FCSTD DOCUMENT  (FreeCAD 1.0R39319 (Git))
Label: assembly
License: All rights reserved
LicenseURL: https://en.wikipedia.org/wiki/All_rights_reserved
objects: App::FeaturePython×60, App::Link×19, Assembly::JointGroup×1, Assembly::AssemblyObject×1
EXTERNAL_REF file=bottom.FCStd obj=Body
EXTERNAL_REF file=side.FCStd obj=Body
EXTERNAL_REF file=speaker_panel.FCStd obj=Body
EXTERNAL_REF file=top.FCStd obj=Body
EXTERNAL_REF file=marquee.FCStd obj=Body
EXTERNAL_REF file=glass.FCStd obj=Body
EXTERNAL_REF file=front.FCStd obj=Body
EXTERNAL_REF file=fan_plane.FCStd obj=Body
EXTERNAL_REF file=ctrl_panel_front.FCStd obj=Body
EXTERNAL_REF file=ctrl_panel_bottom.FCStd obj=Body
EXTERNAL_REF file=control_panel.FCStd obj=Body
EXTERNAL_REF file=connector_panel.FCStd obj=Body
EXTERNAL_REF file=back_top_door.FCStd obj=Body
EXTERNAL_REF file=back_bottom_door.FCStd obj=Body
EXTERNAL_REF file=back_bottom.FCStd obj=Body
EXTERNAL_REF file=internal_plate.FCStd obj=Body
EXTERNAL_REF file=internal_separator.FCStd obj=Body

FEATURE [App::Link] bottom_body  label="bottom"
  LinkPlacement = pos=(397,600,85) rot=(-0.707107,0.707107,0;3.14159rad)
  LinkedObject = -> <external bottom.FCStd>#Body
  Placement = pos=(397,600,85) rot=(-0.707107,0.707107,0;3.14159rad)
FEATURE [App::Link] side_body  label="side_left"
  LinkedObject = -> <external side.FCStd>#Body
FEATURE [App::Link] speaker_panel_body  label="speaker_panel"
  LinkPlacement = pos=(345.457,-1.59533e-10,1534.51) rot=(-0.086827,-0.086827,0.992433;1.57839rad)
  LinkedObject = -> <external speaker_panel.FCStd>#Body
  Placement = pos=(345.457,-1.59533e-10,1534.51) rot=(-0.086827,-0.086827,0.992433;1.57839rad)
FEATURE [App::Link] top_body  label="top"
  LinkPlacement = pos=(147.687,600,1677) rot=(0,0,1;4.71239rad)
  LinkedObject = -> <external top.FCStd>#Body
  Placement = pos=(147.687,600,1677) rot=(0,0,1;4.71239rad)
FEATURE [App::Link] marquee_body  label="marquee"
  LinkPlacement = pos=(316.805,600,1697) rot=(-0.540716,0.540716,-0.6444;1.99673rad)
  LinkedObject = -> <external marquee.FCStd>#Body
  Placement = pos=(316.805,600,1697) rot=(-0.540716,0.540716,-0.6444;1.99673rad)
FEATURE [App::Link] Body  label="glass"
  LinkPlacement = pos=(382.714,600,967.037) rot=(0.633338,-0.633338,-0.444709;2.3047rad)
  LinkedObject = -> <external glass.FCStd>#Body
  Placement = pos=(382.714,600,967.037) rot=(0.633338,-0.633338,-0.444709;2.3047rad)
FEATURE [App::Link] front_body  label="front"
  LinkPlacement = pos=(412,-8.88241e-11,855) rot=(0,1,0;3.14159rad)
  LinkedObject = -> <external front.FCStd>#Body
  Placement = pos=(412,-8.88241e-11,855) rot=(0,1,0;3.14159rad)
FEATURE [App::Link] fan_plane_body  label="fan_plane"
  LinkPlacement = pos=(23.5142,600,1546.61) rot=(-0.357407,0.357407,0.862856;4.56541rad)
  LinkedObject = -> <external fan_plane.FCStd>#Body
  Placement = pos=(23.5142,600,1546.61) rot=(-0.357407,0.357407,0.862856;4.56541rad)
FEATURE [App::Link] ctrl_panel_body  label="ctrl_panel_front"
  LinkPlacement = pos=(551.849,600,852.879) rot=(-0.548043,0.548043,0.631899;4.26868rad)
  LinkedObject = -> <external ctrl_panel_front.FCStd>#Body
  Placement = pos=(551.849,600,852.879) rot=(-0.548043,0.548043,0.631899;4.26868rad)
FEATURE [App::Link] ctrl_panel_body001  label="ctrl_panel_bottom"
  LinkPlacement = pos=(397,600,855) rot=(0,0,1;4.71239rad)
  LinkedObject = -> <external ctrl_panel_bottom.FCStd>#Body
  Placement = pos=(397,600,855) rot=(0,0,1;4.71239rad)
FEATURE [App::Link] Body001  label="control_panel"
  LinkPlacement = pos=(568.82,-1.01012e-10,971.673) rot=(0.070712,0.070712,0.994987;1.57582rad)
  LinkedObject = -> <external control_panel.FCStd>#Body
  Placement = pos=(568.82,-1.01012e-10,971.673) rot=(0.070712,0.070712,0.994987;1.57582rad)
FEATURE [App::Link] connector_panel_body  label="connector_panel"
  LinkPlacement = pos=(17,-1.1304e-10,1086.61) rot=(0,1,0;3.14159rad)
  LinkedObject = -> <external connector_panel.FCStd>#Body
  Placement = pos=(17,-1.1304e-10,1086.61) rot=(0,1,0;3.14159rad)
FEATURE [App::FeaturePython] GroundedJoint  # Assembly grounded joint (typed FeaturePython)
  ObjectToGround = -> side_body
FEATURE [App::FeaturePython] Joint  label="Distance"  # Assembly joint (typed FeaturePython)
  Activated = true
  AngleMax = 0
  AngleMin = 0
  Detach1 = false
  Detach2 = false
  Distance = 0
  Distance2 = 0
  EnableAngleMax = false
  EnableAngleMin = false
  EnableLengthMax = false
  EnableLengthMin = false
  JointType = 5 (Distance)
  LengthMax = 0
  LengthMin = 0
  Placement1 = pos=(600,85,4.93758) rot=(-0.57735,-0.57735,0.57735;2.0944rad)
  Placement2 = pos=(224.254,-8.01027e-11,770.624) rot=(-0.57735,-0.57735,-0.57735;2.0944rad)
  Reference1 = -> Assembly [marquee_body.Face5,marquee_body.Face5]
  Reference2 = -> Assembly [side_body.Face2,side_body.Face2]
FEATURE [App::FeaturePython] Joint001  label="Parallel"  # Assembly joint (typed FeaturePython)
  Activated = true
  AngleMax = 0
  AngleMin = 0
  Detach1 = false
  Detach2 = false
  Distance = 0
  Distance2 = 0
  EnableAngleMax = false
  EnableAngleMin = false
  EnableLengthMax = false
  EnableLengthMin = false
  JointType = 6 (Parallel)
  LengthMax = 0
  LengthMin = 0
  Placement1 = pos=(346.37,-8,1615.71) rot=(0,1,0;1.39626rad)
  Placement2 = pos=(300,85,10) rot=(0,0,1;0rad)
  Reference1 = -> Assembly [side_body.Face23,side_body.Face23]
  Reference2 = -> Assembly [marquee_body.Face8,marquee_body.Face8]
FEATURE [App::FeaturePython] Joint002  label="Distance001"  # Assembly joint (typed FeaturePython)
  Activated = true
  AngleMax = 0
  AngleMin = 0
  Detach1 = false
  Detach2 = false
  Distance = -5
  Distance2 = 0
  EnableAngleMax = false
  EnableAngleMin = false
  EnableLengthMax = false
  EnableLengthMin = false
  JointType = 5 (Distance)
  LengthMax = 0
  LengthMin = 0
  Placement1 = pos=(346.37,-8,1615.71) rot=(0,1,0;1.39626rad)
  Placement2 = pos=(300,85,10) rot=(0,0,1;0rad)
  Reference1 = -> Assembly [side_body.Face23,side_body.Face23]
  Reference2 = -> Assembly [marquee_body.Face8,marquee_body.Face8]
FEATURE [App::FeaturePython] Joint003  label="Distance002"  # Assembly joint (typed FeaturePython)
  Activated = true
  AngleMax = 0
  AngleMin = 0
  Detach1 = false
  Detach2 = false
  Distance = -3
  Distance2 = 0
  EnableAngleMax = false
  EnableAngleMin = false
  EnableLengthMax = false
  EnableLengthMin = false
  JointType = 5 (Distance)
  LengthMax = 0
  LengthMin = 0
  Placement1 = pos=(235.443,-8,1700) rot=(0,0,1;0rad)
  Placement2 = pos=(300,2.274e-13,-1.137e-13) rot=(0.707107,0,0.707107;3.14159rad)
  Reference1 = -> Assembly [side_body.Face19,side_body.Face19]
  Reference2 = -> Assembly [marquee_body.Edge3,marquee_body.Edge3]
FEATURE [App::FeaturePython] Joint004  label="Distance003"  # Assembly joint (typed FeaturePython)
  Activated = true
  AngleMax = 0
  AngleMin = 0
  Detach1 = false
  Detach2 = false
  Distance = 0
  Distance2 = 0
  EnableAngleMax = false
  EnableAngleMin = false
  EnableLengthMax = false
  EnableLengthMin = false
  JointType = 5 (Distance)
  LengthMax = 0
  LengthMin = 0
  Placement1 = pos=(224.254,-8.01027e-11,770.624) rot=(-0.57735,-0.57735,-0.57735;2.0944rad)
  Placement2 = pos=(600,85,7.5) rot=(-0.57735,-0.57735,0.57735;2.0944rad)
  Reference1 = -> Assembly [side_body.Face2,side_body.Face2]
  Reference2 = -> Assembly [top_body.Face2,top_body.Face2]
FEATURE [App::FeaturePython] Joint005  label="Parallel001"  # Assembly joint (typed FeaturePython)
  Activated = true
  AngleMax = 0
  AngleMin = 0
  Detach1 = false
  Detach2 = false
  Distance = 0
  Distance2 = 0
  EnableAngleMax = false
  EnableAngleMin = false
  EnableLengthMax = false
  EnableLengthMin = false
  JointType = 6 (Parallel)
  LengthMax = 0
  LengthMin = 0
  Placement1 = pos=(300,85,15) rot=(0,0,1;0rad)
  Placement2 = pos=(235.443,-8,1700) rot=(0,0,1;0rad)
  Reference1 = -> Assembly [top_body.Face6,top_body.Face6]
  Reference2 = -> Assembly [side_body.Face19,side_body.Face19]
FEATURE [App::FeaturePython] Joint006  label="Distance004"  # Assembly joint (typed FeaturePython)
  Activated = true
  AngleMax = 0
  AngleMin = 0
  Detach1 = false
  Detach2 = false
  Distance = 8
  Distance2 = 0
  EnableAngleMax = false
  EnableAngleMin = false
  EnableLengthMax = false
  EnableLengthMin = false
  JointType = 5 (Distance)
  LengthMax = 0
  LengthMin = 0
  Placement1 = pos=(300,85,15) rot=(0,0,1;0rad)
  Placement2 = pos=(235.443,-8,1700) rot=(0,0,1;0rad)
  Reference1 = -> Assembly [top_body.Face6,top_body.Face6]
  Reference2 = -> Assembly [side_body.Face19,side_body.Face19]
FEATURE [App::FeaturePython] Joint007  label="Distance005"  # Assembly joint (typed FeaturePython)
  Activated = true
  AngleMax = 0
  AngleMin = 0
  Detach1 = false
  Detach2 = false
  Distance = 0
  Distance2 = 0
  EnableAngleMax = false
  EnableAngleMin = false
  EnableLengthMax = false
  EnableLengthMin = false
  JointType = 5 (Distance)
  LengthMax = 0
  LengthMin = 0
  Placement1 = pos=(300,85,0) rot=(0,0,1;0rad)
  Placement2 = pos=(300,170,15) rot=(-0.707107,0,0.707107;3.14159rad)
  Reference1 = -> Assembly [marquee_body.Face4,marquee_body.Face4]
  Reference2 = -> Assembly [top_body.Edge10,top_body.Edge10]
FEATURE [App::FeaturePython] Joint008  label="Distance006"  # Assembly joint (typed FeaturePython)
  Activated = true
  AngleMax = 0
  AngleMin = 0
  Detach1 = false
  Detach2 = false
  Distance = 0
  Distance2 = 0
  EnableAngleMax = false
  EnableAngleMin = false
  EnableLengthMax = false
  EnableLengthMin = false
  JointType = 5 (Distance)
  LengthMax = 0
  LengthMin = 0
  Placement1 = pos=(4.4e-15,80,7.5) rot=(-0.57735,0.57735,-0.57735;2.0944rad)
  Placement2 = pos=(224.254,-8.01027e-11,770.624) rot=(-0.57735,-0.57735,-0.57735;2.0944rad)
  Reference1 = -> Assembly [speaker_panel_body.Face4,speaker_panel_body.Face4]
  Reference2 = -> Assembly [side_body.Face2,side_body.Face2]
FEATURE [App::FeaturePython] Joint009  label="Distance007"  # Assembly joint (typed FeaturePython)
  Activated = true
  AngleMax = 0
  AngleMin = 0
  Detach1 = false
  Detach2 = false
  Distance = 0
  Distance2 = 0
  EnableAngleMax = false
  EnableAngleMin = false
  EnableLengthMax = false
  EnableLengthMin = false
  JointType = 5 (Distance)
  LengthMax = 0
  LengthMin = 0
  Placement1 = pos=(300,85,0) rot=(0,0,1;0rad)
  Placement2 = pos=(300,0,7.5) rot=(1,0,0;4.71239rad)
  Reference1 = -> Assembly [marquee_body.Face4,marquee_body.Face4]
  Reference2 = -> Assembly [speaker_panel_body.Face1,speaker_panel_body.Face1]
FEATURE [App::FeaturePython] Joint010  label="Distance008"  # Assembly joint (typed FeaturePython)
  Activated = true
  AngleMax = 0
  AngleMin = 0
  Detach1 = false
  Detach2 = false
  Distance = -5
  Distance2 = 0
  EnableAngleMax = false
  EnableAngleMin = false
  EnableLengthMax = false
  EnableLengthMin = false
  JointType = 5 (Distance)
  LengthMax = 0
  LengthMin = 0
  Placement1 = pos=(300,81.1697,-2.274e-13) rot=(0,0,1;0rad)
  Placement2 = pos=(300,170,-1.137e-13) rot=(-0.707107,0,0.707107;3.14159rad)
  Reference1 = -> Assembly [speaker_panel_body.Face7,speaker_panel_body.Face7]
  Reference2 = -> Assembly [marquee_body.Edge13,marquee_body.Edge13]
FEATURE [App::FeaturePython] Joint011  label="Distance009"  # Assembly joint (typed FeaturePython)
  Activated = true
  AngleMax = 0
  AngleMin = 0
  Detach1 = false
  Detach2 = false
  Distance = 0
  Distance2 = 0
  EnableAngleMax = false
  EnableAngleMin = false
  EnableLengthMax = false
  EnableLengthMin = false
  JointType = 5 (Distance)
  LengthMax = 0
  LengthMin = 0
  Placement1 = pos=(600,90,7.5) rot=(0.57735,0.57735,-0.57735;4.18879rad)
  Placement2 = pos=(224.254,-8.01027e-11,770.624) rot=(-0.57735,-0.57735,-0.57735;2.0944rad)
  Reference1 = -> Assembly [fan_plane_body.Face2,fan_plane_body.Face2]
  Reference2 = -> Assembly [side_body.Face2,side_body.Face2]
FEATURE [App::FeaturePython] Joint012  label="Parallel002"  # Assembly joint (typed FeaturePython)
  Activated = true
  AngleMax = 0
  AngleMin = 0
  Detach1 = false
  Detach2 = false
  Distance = 0
  Distance2 = 0
  EnableAngleMax = false
  EnableAngleMin = false
  EnableLengthMax = false
  EnableLengthMin = false
  JointType = 6 (Parallel)
  LengthMax = 0
  LengthMin = 0
  Placement1 = pos=(300,90,15) rot=(0,0,1;0rad)
  Placement2 = pos=(75,-8,1625) rot=(0,-1,0;0.785398rad)
  Reference1 = -> Assembly [fan_plane_body.Face8,fan_plane_body.Face8]
  Reference2 = -> Assembly [side_body.Face15,side_body.Face15]
FEATURE [App::FeaturePython] Joint013  label="Distance010"  # Assembly joint (typed FeaturePython)
  Activated = true
  AngleMax = 0
  AngleMin = 0
  Detach1 = false
  Detach2 = false
  Distance = 0
  Distance2 = 0
  EnableAngleMax = false
  EnableAngleMin = false
  EnableLengthMax = false
  EnableLengthMin = false
  JointType = 5 (Distance)
  LengthMax = 0
  LengthMin = 0
  Placement1 = pos=(300,90,15) rot=(0,0,1;0rad)
  Placement2 = pos=(300,0,15) rot=(0.707107,0,0.707107;3.14159rad)
  Reference1 = -> Assembly [fan_plane_body.Face8,fan_plane_body.Face8]
  Reference2 = -> Assembly [top_body.Edge4,top_body.Edge4]
FEATURE [App::FeaturePython] Joint014  label="Distance011"  # Assembly joint (typed FeaturePython)
  Activated = true
  AngleMax = 0
  AngleMin = 0
  Detach1 = false
  Detach2 = false
  Distance = 0
  Distance2 = 0
  EnableAngleMax = false
  EnableAngleMin = false
  EnableLengthMax = false
  EnableLengthMin = false
  JointType = 5 (Distance)
  LengthMax = 0
  LengthMin = 0
  Placement1 = pos=(300,180,7.5) rot=(0,-0.707107,0.707107;3.14159rad)
  Placement2 = pos=(300,0,0) rot=(0.707107,0,0.707107;3.14159rad)
  Reference1 = -> Assembly [fan_plane_body.Face3,fan_plane_body.Face3]
  Reference2 = -> Assembly [top_body.Edge3,top_body.Edge3]
FEATURE [App::FeaturePython] Joint015  label="Distance012"  # Assembly joint (typed FeaturePython)
  Activated = true
  AngleMax = 0
  AngleMin = 0
  Detach1 = false
  Detach2 = false
  Distance = 0
  Distance2 = 0
  EnableAngleMax = false
  EnableAngleMin = false
  EnableLengthMax = false
  EnableLengthMin = false
  JointType = 5 (Distance)
  LengthMax = 0
  LengthMin = 0
  Placement1 = pos=(600,190,7.5) rot=(0.57735,0.57735,-0.57735;4.18879rad)
  Placement2 = pos=(224.254,-8.01027e-11,770.624) rot=(-0.57735,-0.57735,-0.57735;2.0944rad)
  Reference1 = -> Assembly [bottom_body.Face2,bottom_body.Face2]
  Reference2 = -> Assembly [side_body.Face2,side_body.Face2]
FEATURE [App::FeaturePython] Joint016  label="Distance013"  # Assembly joint (typed FeaturePython)
  Activated = true
  AngleMax = 0
  AngleMin = 0
  Detach1 = false
  Detach2 = false
  Distance = 70
  Distance2 = 0
  EnableAngleMax = false
  EnableAngleMin = false
  EnableLengthMax = false
  EnableLengthMin = false
  JointType = 5 (Distance)
  LengthMax = 0
  LengthMin = 0
  Placement1 = pos=(300,190,15) rot=(0,0,1;0rad)
  Placement2 = pos=(225.638,-8,-8.278e-13) rot=(0,0,1;0rad)
  Reference1 = -> Assembly [bottom_body.Face6,bottom_body.Face6]
  Reference2 = -> Assembly [side_body.Face7,side_body.Face7]
FEATURE [App::FeaturePython] Joint017  label="Distance014"  # Assembly joint (typed FeaturePython)
  Activated = true
  AngleMax = 0
  AngleMin = 0
  Detach1 = false
  Detach2 = false
  Distance = 0
  Distance2 = 0
  EnableAngleMax = false
  EnableAngleMin = false
  EnableLengthMax = false
  EnableLengthMin = false
  JointType = 5 (Distance)
  LengthMax = 0
  LengthMin = 0
  Placement1 = pos=(7.5,1.6108e-11,150) rot=(0.57735,-0.57735,-0.57735;4.18879rad)
  Placement2 = pos=(224.254,-8.01027e-11,770.624) rot=(-0.57735,-0.57735,-0.57735;2.0944rad)
  Reference1 = -> Assembly [connector_panel_body.Face4,connector_panel_body.Face4]
  Reference2 = -> Assembly [side_body.Face2,side_body.Face2]
FEATURE [App::FeaturePython] Joint019  label="Parallel003"  # Assembly joint (typed FeaturePython)
  Activated = true
  AngleMax = 0
  AngleMin = 0
  Detach1 = false
  Detach2 = false
  Distance = 0
  Distance2 = 0
  EnableAngleMax = false
  EnableAngleMin = false
  EnableLengthMax = false
  EnableLengthMin = false
  JointType = 6 (Parallel)
  LengthMax = 0
  LengthMin = 0
  Placement1 = pos=(15,301.87,151.126) rot=(0.707107,0,0.707107;3.14159rad)
  Placement2 = pos=(0,-8,782.322) rot=(0,-1,0;1.5708rad)
  Reference1 = -> Assembly [connector_panel_body.Face14,connector_panel_body.Face14]
  Reference2 = -> Assembly [side_body.Face11,side_body.Face11]
FEATURE [App::FeaturePython] Joint020  label="Distance016"  # Assembly joint (typed FeaturePython)
  Activated = true
  AngleMax = 0
  AngleMin = 0
  Detach1 = false
  Detach2 = false
  Distance = 0
  Distance2 = 0
  EnableAngleMax = false
  EnableAngleMin = false
  EnableLengthMax = false
  EnableLengthMin = false
  JointType = 5 (Distance)
  LengthMax = 0
  LengthMin = 0
  Placement1 = pos=(300,380,7.5) rot=(0,0.707107,-0.707107;3.14159rad)
  Placement2 = pos=(1.69713e-11,301.87,151.126) rot=(0.707107,0,0.707107;3.14159rad)
  Reference1 = -> Assembly [bottom_body.Face3,bottom_body.Face3]
  Reference2 = -> Assembly [connector_panel_body.Face13,connector_panel_body.Face13]
FEATURE [App::FeaturePython] Joint021  label="Distance017"  # Assembly joint (typed FeaturePython)
  Activated = true
  AngleMax = 0
  AngleMin = 0
  Detach1 = false
  Detach2 = false
  Distance = 0
  Distance2 = 0
  EnableAngleMax = false
  EnableAngleMin = false
  EnableLengthMax = false
  EnableLengthMin = false
  JointType = 5 (Distance)
  LengthMax = 0
  LengthMin = 0
  Placement1 = pos=(7.5,4.71889e-11,425) rot=(0.57735,-0.57735,-0.57735;4.18879rad)
  Placement2 = pos=(224.254,-8.01027e-11,770.624) rot=(-0.57735,-0.57735,-0.57735;2.0944rad)
  Reference1 = -> Assembly [front_body.Face4,front_body.Face4]
  Reference2 = -> Assembly [side_body.Face2,side_body.Face2]
FEATURE [App::FeaturePython] Joint022  label="Distance018"  # Assembly joint (typed FeaturePython)
  Activated = true
  AngleMax = 0
  AngleMin = 0
  Detach1 = false
  Detach2 = false
  Distance = 0
  Distance2 = 0
  EnableAngleMax = false
  EnableAngleMin = false
  EnableLengthMax = false
  EnableLengthMin = false
  JointType = 5 (Distance)
  LengthMax = 0
  LengthMin = 0
  Placement1 = pos=(300,0,7.5) rot=(-1,0,0;1.5708rad)
  Placement2 = pos=(15,300,425) rot=(0.707107,0,0.707107;3.14159rad)
  Reference1 = -> Assembly [bottom_body.Face1,bottom_body.Face1]
  Reference2 = -> Assembly [front_body.Face6,front_body.Face6]
FEATURE [App::FeaturePython] Joint023  label="Distance019"  # Assembly joint (typed FeaturePython)
  Activated = true
  AngleMax = 0
  AngleMin = 0
  Detach1 = false
  Detach2 = false
  Distance = -5
  Distance2 = 0
  EnableAngleMax = false
  EnableAngleMin = false
  EnableLengthMax = false
  EnableLengthMin = false
  JointType = 5 (Distance)
  LengthMax = 0
  LengthMin = 0
  Placement1 = pos=(7.5,300,850) rot=(0.707107,-0.707107,0;3.14159rad)
  Placement2 = pos=(225.638,-8,-8.278e-13) rot=(0,0,1;0rad)
  Reference1 = -> Assembly [front_body.Face3,front_body.Face3]
  Reference2 = -> Assembly [side_body.Face7,side_body.Face7]
FEATURE [App::FeaturePython] Joint024  label="Distance020"  # Assembly joint (typed FeaturePython)
  Activated = true
  AngleMax = 0
  AngleMin = 0
  Detach1 = false
  Detach2 = false
  Distance = 0
  Distance2 = 0
  EnableAngleMax = false
  EnableAngleMin = false
  EnableLengthMax = false
  EnableLengthMin = false
  JointType = 5 (Distance)
  LengthMax = 0
  LengthMin = 0
  Placement1 = pos=(600,70,7.5) rot=(-0.57735,-0.57735,0.57735;2.0944rad)
  Placement2 = pos=(224.254,-8.01027e-11,770.624) rot=(-0.57735,-0.57735,-0.57735;2.0944rad)
  Reference1 = -> Assembly [ctrl_panel_body001.Face2,ctrl_panel_body001.Face2]
  Reference2 = -> Assembly [side_body.Face2,side_body.Face2]
FEATURE [App::FeaturePython] Joint025  label="Distance021"  # Assembly joint (typed FeaturePython)
  Activated = true
  AngleMax = 0
  AngleMin = 0
  Detach1 = false
  Detach2 = false
  Distance = 0
  Distance2 = 0
  EnableAngleMax = false
  EnableAngleMin = false
  EnableLengthMax = false
  EnableLengthMin = false
  JointType = 5 (Distance)
  LengthMax = 0
  LengthMin = 0
  Placement1 = pos=(300,69.7822,0) rot=(0,0,1;0rad)
  Placement2 = pos=(7.5,300,-3.29692e-11) rot=(0,0,1;1.5708rad)
  Reference1 = -> Assembly [ctrl_panel_body001.Face7,ctrl_panel_body001.Face7]
  Reference2 = -> Assembly [front_body.Face1,front_body.Face1]
FEATURE [App::FeaturePython] Joint026  label="Distance022"  # Assembly joint (typed FeaturePython)
  Activated = true
  AngleMax = 0
  AngleMin = 0
  Detach1 = false
  Detach2 = false
  Distance = 0
  Distance2 = 0
  EnableAngleMax = false
  EnableAngleMin = false
  EnableLengthMax = false
  EnableLengthMin = false
  JointType = 5 (Distance)
  LengthMax = 0
  LengthMin = 0
  Placement1 = pos=(300,0,7.5) rot=(-1,0,0;1.5708rad)
  Placement2 = pos=(15,300,425) rot=(0.707107,0,0.707107;3.14159rad)
  Reference1 = -> Assembly [ctrl_panel_body001.Face1,ctrl_panel_body001.Face1]
  Reference2 = -> Assembly [front_body.Face6,front_body.Face6]
FEATURE [App::FeaturePython] Joint027  label="Distance023"  # Assembly joint (typed FeaturePython)
  Activated = true
  AngleMax = 0
  AngleMin = 0
  Detach1 = false
  Detach2 = false
  Distance = 0
  Distance2 = 0
  EnableAngleMax = false
  EnableAngleMin = false
  EnableLengthMax = false
  EnableLengthMin = false
  JointType = 5 (Distance)
  LengthMax = 0
  LengthMin = 0
  Placement1 = pos=(600,60,7.5) rot=(0.57735,0.57735,-0.57735;4.18879rad)
  Placement2 = pos=(224.254,-8.01027e-11,770.624) rot=(-0.57735,-0.57735,-0.57735;2.0944rad)
  Reference1 = -> Assembly [ctrl_panel_body.Face2,ctrl_panel_body.Face2]
  Reference2 = -> Assembly [side_body.Face2,side_body.Face2]
FEATURE [App::FeaturePython] Joint028  label="Parallel024"  # Assembly joint (typed FeaturePython)
  Activated = true
  AngleMax = 0
  AngleMin = 0
  Detach1 = false
  Detach2 = false
  Distance = 0
  Distance2 = 0
  EnableAngleMax = false
  EnableAngleMin = false
  EnableLengthMax = false
  EnableLengthMin = false
  JointType = 6 (Parallel)
  LengthMax = 0
  LengthMin = 0
  Placement1 = pos=(579.262,-8,924.836) rot=(0,-1,0;1.4289rad)
  Placement2 = pos=(299.448,59.4824,1.137e-13) rot=(0,0,1;0rad)
  Reference1 = -> Assembly [side_body.Face10,side_body.Face10]
  Reference2 = -> Assembly [ctrl_panel_body.Face15,ctrl_panel_body.Face15]
FEATURE [App::FeaturePython] Joint029  label="Distance024"  # Assembly joint (typed FeaturePython)
  Activated = true
  AngleMax = 0
  AngleMin = 0
  Detach1 = false
  Detach2 = false
  Distance = 0
  Distance2 = 0
  EnableAngleMax = false
  EnableAngleMin = false
  EnableLengthMax = false
  EnableLengthMin = false
  JointType = 5 (Distance)
  LengthMax = 0
  LengthMin = 0
  Placement1 = pos=(300,69.7822,0) rot=(0,0,1;0rad)
  Placement2 = pos=(300,0,15) rot=(0.707107,0,0.707107;3.14159rad)
  Reference1 = -> Assembly [ctrl_panel_body001.Face7,ctrl_panel_body001.Face7]
  Reference2 = -> Assembly [ctrl_panel_body.Edge4,ctrl_panel_body.Edge4]
FEATURE [App::FeaturePython] Joint030  label="Distance025"  # Assembly joint (typed FeaturePython)
  Activated = true
  AngleMax = 0
  AngleMin = 0
  Detach1 = false
  Detach2 = false
  Distance = 0
  Distance2 = 0
  EnableAngleMax = false
  EnableAngleMin = false
  EnableLengthMax = false
  EnableLengthMin = false
  JointType = 5 (Distance)
  LengthMax = 0
  LengthMin = 0
  Placement1 = pos=(299.448,59.4824,15) rot=(0,0,1;0rad)
  Placement2 = pos=(300,140,0) rot=(-0.707107,0,0.707107;3.14159rad)
  Reference1 = -> Assembly [ctrl_panel_body.Face16,ctrl_panel_body.Face16]
  Reference2 = -> Assembly [ctrl_panel_body001.Edge9,ctrl_panel_body001.Edge9]
FEATURE [App::FeaturePython] Joint031  label="Distance026"  # Assembly joint (typed FeaturePython)
  Activated = true
  AngleMax = 0
  AngleMin = 0
  Detach1 = false
  Detach2 = false
  Distance = 0
  Distance2 = 0
  EnableAngleMax = false
  EnableAngleMin = false
  EnableLengthMax = false
  EnableLengthMin = false
  JointType = 5 (Distance)
  LengthMax = 0
  LengthMin = 0
  Placement1 = pos=(224.254,-8.01027e-11,770.624) rot=(-0.57735,-0.57735,-0.57735;2.0944rad)
  Placement2 = pos=(-2.17e-14,100,7.5) rot=(-0.57735,0.57735,-0.57735;2.0944rad)
  Reference1 = -> Assembly [side_body.Face2,side_body.Face2]
  Reference2 = -> Assembly [Body001.Face4,Body001.Face4]
FEATURE [App::FeaturePython] Joint032  label="Distance027"  # Assembly joint (typed FeaturePython)
  Activated = true
  AngleMax = 0
  AngleMin = 0
  Detach1 = false
  Detach2 = false
  Distance = 0
  Distance2 = 0
  EnableAngleMax = false
  EnableAngleMin = false
  EnableLengthMax = false
  EnableLengthMin = false
  JointType = 5 (Distance)
  LengthMax = 0
  LengthMin = 0
  Placement1 = pos=(300,120,7.5) rot=(0,-0.707107,0.707107;3.14159rad)
  Placement2 = pos=(298.348,98.9763,0) rot=(0,0,1;0rad)
  Reference1 = -> Assembly [ctrl_panel_body.Face3,ctrl_panel_body.Face3]
  Reference2 = -> Assembly [Body001.Face19,Body001.Face19]
FEATURE [App::FeaturePython] Joint033  label="Distance028"  # Assembly joint (typed FeaturePython)
  Activated = true
  AngleMax = 0
  AngleMin = 0
  Detach1 = false
  Detach2 = false
  Distance = 0
  Distance2 = 0
  EnableAngleMax = false
  EnableAngleMin = false
  EnableLengthMax = false
  EnableLengthMin = false
  JointType = 5 (Distance)
  LengthMax = 0
  LengthMin = 0
  Placement1 = pos=(299.448,59.4824,1.137e-13) rot=(0,0,1;0rad)
  Placement2 = pos=(300,5.68e-14,7.5) rot=(-1,0,0;1.5708rad)
  Reference1 = -> Assembly [ctrl_panel_body.Face15,ctrl_panel_body.Face15]
  Reference2 = -> Assembly [Body001.Face1,Body001.Face1]
FEATURE [App::FeaturePython] Joint034  label="Distance029"  # Assembly joint (typed FeaturePython)
  Activated = true
  AngleMax = 0
  AngleMin = 0
  Detach1 = false
  Detach2 = false
  Distance = 2
  Distance2 = 0
  EnableAngleMax = false
  EnableAngleMin = false
  EnableLengthMax = false
  EnableLengthMin = false
  JointType = 5 (Distance)
  LengthMax = 0
  LengthMin = 0
  Placement1 = pos=(15,301.87,151.126) rot=(0.707107,0,0.707107;3.14159rad)
  Placement2 = pos=(0,-8,782.322) rot=(0,-1,0;1.5708rad)
  Reference1 = -> Assembly [connector_panel_body.Face14,connector_panel_body.Face14]
  Reference2 = -> Assembly [side_body.Face11,side_body.Face11]
FEATURE [App::FeaturePython] Joint035  label="Distance030"  # Assembly joint (typed FeaturePython)
  Activated = true
  AngleMax = 0
  AngleMin = 0
  Detach1 = false
  Detach2 = false
  Distance = 0
  Distance2 = 0
  EnableAngleMax = false
  EnableAngleMin = false
  EnableLengthMax = false
  EnableLengthMin = false
  JointType = 5 (Distance)
  LengthMax = 0
  LengthMin = 0
  Placement1 = pos=(224.254,-8.01027e-11,770.624) rot=(-0.57735,-0.57735,-0.57735;2.0944rad)
  Placement2 = pos=(600,310,3) rot=(0.57735,0.57735,-0.57735;4.18879rad)
  Reference1 = -> Assembly [side_body.Face2,side_body.Face2]
  Reference2 = -> Assembly [Body.Face2,Body.Face2]
FEATURE [App::FeaturePython] Joint036  label="Distance031"  # Assembly joint (typed FeaturePython)
  Activated = true
  AngleMax = 0
  AngleMin = 0
  Detach1 = false
  Detach2 = false
  Distance = 0
  Distance2 = 0
  EnableAngleMax = false
  EnableAngleMin = false
  EnableLengthMax = false
  EnableLengthMin = false
  JointType = 5 (Distance)
  LengthMax = 0
  LengthMin = 0
  Placement1 = pos=(300,310,0) rot=(0,0,1;0rad)
  Placement2 = pos=(300,160,0) rot=(-0.707107,0,0.707107;3.14159rad)
  Reference1 = -> Assembly [Body.Face9,Body.Face9]
  Reference2 = -> Assembly [speaker_panel_body.Edge9,speaker_panel_body.Edge9]
FEATURE [App::FeaturePython] Joint037  label="Distance032"  # Assembly joint (typed FeaturePython)
  Activated = true
  AngleMax = 0
  AngleMin = 0
  Detach1 = false
  Detach2 = false
  Distance = 0
  Distance2 = 0
  EnableAngleMax = false
  EnableAngleMin = false
  EnableLengthMax = false
  EnableLengthMin = false
  JointType = 5 (Distance)
  LengthMax = 0
  LengthMin = 0
  Placement1 = pos=(300,310,0) rot=(0,0,1;0rad)
  Placement2 = pos=(300,200,0) rot=(-0.707107,0,0.707107;3.14159rad)
  Reference1 = -> Assembly [Body.Face9,Body.Face9]
  Reference2 = -> Assembly [Body001.Edge9,Body001.Edge9]
FEATURE [App::Link] Body002  label="back_top_door"
  LinkPlacement = pos=(17,-1.6069e-10,1546.61) rot=(0.707107,0.707107,0;3.14159rad)
  LinkedObject = -> <external back_top_door.FCStd>#Body
  Placement = pos=(17,-1.6069e-10,1546.61) rot=(0.707107,0.707107,0;3.14159rad)
FEATURE [App::FeaturePython] Joint039  label="Distance034"  # Assembly joint (typed FeaturePython)
  Activated = true
  AngleMax = 0
  AngleMin = 0
  Detach1 = false
  Detach2 = false
  Distance = 0
  Distance2 = 0
  EnableAngleMax = false
  EnableAngleMin = false
  EnableLengthMax = false
  EnableLengthMin = false
  JointType = 5 (Distance)
  LengthMax = 0
  LengthMin = 0
  Placement1 = pos=(0,-7.5,230) rot=(0,-1,0;4.71239rad)
  Placement2 = pos=(224.254,-8.01027e-11,770.624) rot=(-0.57735,-0.57735,-0.57735;2.0944rad)
  Reference1 = -> Assembly [Body002.Face4,Body002.Face4]
  Reference2 = -> Assembly [side_body.Face2,side_body.Face2]
FEATURE [App::FeaturePython] Joint040  label="Distance035"  # Assembly joint (typed FeaturePython)
  Activated = true
  AngleMax = 0
  AngleMin = 0
  Detach1 = false
  Detach2 = false
  Distance = 0
  Distance2 = 0
  EnableAngleMax = false
  EnableAngleMin = false
  EnableLengthMax = false
  EnableLengthMin = false
  JointType = 5 (Distance)
  LengthMax = 0
  LengthMin = 0
  Placement1 = pos=(300,-15,230) rot=(-0.57735,-0.57735,-0.57735;2.0944rad)
  Placement2 = pos=(15,301.87,151.126) rot=(0.707107,0,0.707107;3.14159rad)
  Reference1 = -> Assembly [Body002.Face6,Body002.Face6]
  Reference2 = -> Assembly [connector_panel_body.Face14,connector_panel_body.Face14]
FEATURE [App::FeaturePython] Joint041  label="Distance036"  # Assembly joint (typed FeaturePython)
  Activated = true
  AngleMax = 0
  AngleMin = 0
  Detach1 = false
  Detach2 = false
  Distance = 0
  Distance2 = 0
  EnableAngleMax = false
  EnableAngleMin = false
  EnableLengthMax = false
  EnableLengthMin = false
  JointType = 5 (Distance)
  LengthMax = 0
  LengthMin = 0
  Placement1 = pos=(300,-7.5,0) rot=(0,0,1;0rad)
  Placement2 = pos=(300,0,0) rot=(0.707107,0,0.707107;3.14159rad)
  Reference1 = -> Assembly [Body002.Face1,Body002.Face1]
  Reference2 = -> Assembly [fan_plane_body.Edge3,fan_plane_body.Edge3]
FEATURE [App::FeaturePython] Joint042  label="Distance037"  # Assembly joint (typed FeaturePython)
  Activated = true
  AngleMax = 0
  AngleMin = 0
  Detach1 = false
  Detach2 = false
  Distance = 0
  Distance2 = 0
  EnableAngleMax = false
  EnableAngleMin = false
  EnableLengthMax = false
  EnableLengthMin = false
  JointType = 5 (Distance)
  LengthMax = 0
  LengthMin = 0
  Placement1 = pos=(7.5,300,-3.29692e-11) rot=(0,0,1;1.5708rad)
  Placement2 = pos=(300,-7.5,460) rot=(0,-1,0;3.14159rad)
  Reference1 = -> Assembly [connector_panel_body.Face1,connector_panel_body.Face1]
  Reference2 = -> Assembly [Body002.Face3,Body002.Face3]
FEATURE [App::Link] back_bottom_door_body  label="back_bottom_door"
  LinkPlacement = pos=(17,-8.17396e-11,786.614) rot=(0.707107,0.707107,0;3.14159rad)
  LinkedObject = -> <external back_bottom_door.FCStd>#Body
  Placement = pos=(17,-8.17396e-11,786.614) rot=(0.707107,0.707107,0;3.14159rad)
FEATURE [App::FeaturePython] Joint043  label="Distance038"  # Assembly joint (typed FeaturePython)
  Activated = true
  AngleMax = 0
  AngleMin = 0
  Detach1 = false
  Detach2 = false
  Distance = 0
  Distance2 = 0
  EnableAngleMax = false
  EnableAngleMin = false
  EnableLengthMax = false
  EnableLengthMin = false
  JointType = 5 (Distance)
  LengthMax = 0
  LengthMin = 0
  Placement1 = pos=(0,-7.5,215) rot=(0,-1,0;4.71239rad)
  Placement2 = pos=(224.254,-8.01027e-11,770.624) rot=(-0.57735,-0.57735,-0.57735;2.0944rad)
  Reference1 = -> Assembly [back_bottom_door_body.Face4,back_bottom_door_body.Face4]
  Reference2 = -> Assembly [side_body.Face2,side_body.Face2]
FEATURE [App::FeaturePython] Joint044  label="Distance039"  # Assembly joint (typed FeaturePython)
  Activated = true
  AngleMax = 0
  AngleMin = 0
  Detach1 = false
  Detach2 = false
  Distance = 0
  Distance2 = 0
  EnableAngleMax = false
  EnableAngleMin = false
  EnableLengthMax = false
  EnableLengthMin = false
  JointType = 5 (Distance)
  LengthMax = 0
  LengthMin = 0
  Placement1 = pos=(300,-15,215) rot=(-0.57735,-0.57735,-0.57735;2.0944rad)
  Placement2 = pos=(15,301.87,151.126) rot=(0.707107,0,0.707107;3.14159rad)
  Reference1 = -> Assembly [back_bottom_door_body.Face6,back_bottom_door_body.Face6]
  Reference2 = -> Assembly [connector_panel_body.Face14,connector_panel_body.Face14]
FEATURE [App::FeaturePython] Joint045  label="Distance040"  # Assembly joint (typed FeaturePython)
  Activated = true
  AngleMax = 0
  AngleMin = 0
  Detach1 = false
  Detach2 = false
  Distance = 0
  Distance2 = 0
  EnableAngleMax = false
  EnableAngleMin = false
  EnableLengthMax = false
  EnableLengthMin = false
  JointType = 5 (Distance)
  LengthMax = 0
  LengthMin = 0
  Placement1 = pos=(7.5,300,300) rot=(0.707107,-0.707107,0;3.14159rad)
  Placement2 = pos=(300,-7.5,0) rot=(0,0,1;0rad)
  Reference1 = -> Assembly [connector_panel_body.Face3,connector_panel_body.Face3]
  Reference2 = -> Assembly [back_bottom_door_body.Face1,back_bottom_door_body.Face1]
FEATURE [App::Link] back_bottom_body  label="back_subwoffer_door"
  LinkPlacement = pos=(17,-3.70479e-11,356.614) rot=(0.707107,0.707107,0;3.14159rad)
  LinkedObject = -> <external back_bottom.FCStd>#Body
  Placement = pos=(17,-3.70479e-11,356.614) rot=(0.707107,0.707107,0;3.14159rad)
FEATURE [App::FeaturePython] Joint046  label="Distance041"  # Assembly joint (typed FeaturePython)
  Activated = true
  AngleMax = 0
  AngleMin = 0
  Detach1 = false
  Detach2 = false
  Distance = 0
  Distance2 = 0
  EnableAngleMax = false
  EnableAngleMin = false
  EnableLengthMax = false
  EnableLengthMin = false
  JointType = 5 (Distance)
  LengthMax = 0
  LengthMin = 0
  Placement1 = pos=(0,-7.5,145) rot=(0,-1,0;4.71239rad)
  Placement2 = pos=(224.254,-8.01027e-11,770.624) rot=(-0.57735,-0.57735,-0.57735;2.0944rad)
  Reference1 = -> Assembly [back_bottom_body.Face4,back_bottom_body.Face4]
  Reference2 = -> Assembly [side_body.Face2,side_body.Face2]
FEATURE [App::FeaturePython] Joint047  label="Distance042"  # Assembly joint (typed FeaturePython)
  Activated = true
  AngleMax = 0
  AngleMin = 0
  Detach1 = false
  Detach2 = false
  Distance = 0
  Distance2 = 0
  EnableAngleMax = false
  EnableAngleMin = false
  EnableLengthMax = false
  EnableLengthMin = false
  JointType = 5 (Distance)
  LengthMax = 0
  LengthMin = 0
  Placement1 = pos=(300,-7.5,0) rot=(0,0,1;0rad)
  Placement2 = pos=(300,-7.5,430) rot=(0,-1,0;3.14159rad)
  Reference1 = -> Assembly [back_bottom_body.Face1,back_bottom_body.Face1]
  Reference2 = -> Assembly [back_bottom_door_body.Face3,back_bottom_door_body.Face3]
FEATURE [App::FeaturePython] Joint048  label="Distance043"  # Assembly joint (typed FeaturePython)
  Activated = true
  AngleMax = 0
  AngleMin = 0
  Detach1 = false
  Detach2 = false
  Distance = 0
  Distance2 = 0
  EnableAngleMax = false
  EnableAngleMin = false
  EnableLengthMax = false
  EnableLengthMin = false
  JointType = 5 (Distance)
  LengthMax = 0
  LengthMin = 0
  Placement1 = pos=(300,-15,145) rot=(-0.57735,-0.57735,-0.57735;2.0944rad)
  Placement2 = pos=(300,-15,215) rot=(-0.57735,-0.57735,-0.57735;2.0944rad)
  Reference1 = -> Assembly [back_bottom_body.Face6,back_bottom_body.Face6]
  Reference2 = -> Assembly [back_bottom_door_body.Face6,back_bottom_door_body.Face6]
FEATURE [App::Link] internal_plate_body  label="internal_plate"
  LinkPlacement = pos=(397,-8.2639e-11,795) rot=(-0.57735,-0.57735,0.57735;2.0944rad)
  LinkedObject = -> <external internal_plate.FCStd>#Body
  Placement = pos=(397,-8.2639e-11,795) rot=(-0.57735,-0.57735,0.57735;2.0944rad)
FEATURE [App::FeaturePython] Joint049  label="Distance044"  # Assembly joint (typed FeaturePython)
  Activated = true
  AngleMax = 0
  AngleMin = 0
  Detach1 = false
  Detach2 = false
  Distance = 0
  Distance2 = 0
  EnableAngleMax = false
  EnableAngleMin = false
  EnableLengthMax = false
  EnableLengthMin = false
  JointType = 5 (Distance)
  LengthMax = 0
  LengthMin = 0
  Placement1 = pos=(-3.75e-14,-7.5,110) rot=(0,-1,0;4.71239rad)
  Placement2 = pos=(224.254,-8.01027e-11,770.624) rot=(-0.57735,-0.57735,-0.57735;2.0944rad)
  Reference1 = -> Assembly [internal_plate_body.Face4,internal_plate_body.Face4]
  Reference2 = -> Assembly [side_body.Face2,side_body.Face2]
FEATURE [App::FeaturePython] Joint050  label="Distance045"  # Assembly joint (typed FeaturePython)
  Activated = true
  AngleMax = 0
  AngleMin = 0
  Detach1 = false
  Detach2 = false
  Distance = -60
  Distance2 = 0
  EnableAngleMax = false
  EnableAngleMin = false
  EnableLengthMax = false
  EnableLengthMin = false
  JointType = 5 (Distance)
  LengthMax = 0
  LengthMin = 0
  Placement1 = pos=(300,-15,110) rot=(-0.57735,-0.57735,-0.57735;2.0944rad)
  Placement2 = pos=(300,69.7822,15) rot=(0,0,1;0rad)
  Reference1 = -> Assembly [internal_plate_body.Face6,internal_plate_body.Face6]
  Reference2 = -> Assembly [ctrl_panel_body001.Face8,ctrl_panel_body001.Face8]
FEATURE [App::FeaturePython] Joint051  label="Distance046"  # Assembly joint (typed FeaturePython)
  Activated = true
  AngleMax = 0
  AngleMin = 0
  Detach1 = false
  Detach2 = false
  Distance = 0
  Distance2 = 0
  EnableAngleMax = false
  EnableAngleMin = false
  EnableLengthMax = false
  EnableLengthMin = false
  JointType = 5 (Distance)
  LengthMax = 0
  LengthMin = 0
  Placement1 = pos=(300,-7.5,1.137e-13) rot=(0,0,1;0rad)
  Placement2 = pos=(15,300,425) rot=(0.707107,0,0.707107;3.14159rad)
  Reference1 = -> Assembly [internal_plate_body.Face1,internal_plate_body.Face1]
  Reference2 = -> Assembly [front_body.Face6,front_body.Face6]
FEATURE [App::Link] internal_separator_body  label="internal_separator"
  LinkPlacement = pos=(192,-8.26865e-11,795) rot=(0.707107,0.707107,0;3.14159rad)
  LinkedObject = -> <external internal_separator.FCStd>#Body
  Placement = pos=(192,-8.26865e-11,795) rot=(0.707107,0.707107,0;3.14159rad)
FEATURE [App::FeaturePython] Joint052  label="Distance047"  # Assembly joint (typed FeaturePython)
  Activated = true
  AngleMax = 0
  AngleMin = 0
  Detach1 = false
  Detach2 = false
  Distance = 0
  Distance2 = 0
  EnableAngleMax = false
  EnableAngleMin = false
  EnableLengthMax = false
  EnableLengthMin = false
  JointType = 5 (Distance)
  LengthMax = 0
  LengthMin = 0
  Placement1 = pos=(0,-7.5,250) rot=(0,-1,0;4.71239rad)
  Placement2 = pos=(224.254,-8.01027e-11,770.624) rot=(-0.57735,-0.57735,-0.57735;2.0944rad)
  Reference1 = -> Assembly [internal_separator_body.Face4,internal_separator_body.Face4]
  Reference2 = -> Assembly [side_body.Face2,side_body.Face2]
FEATURE [App::FeaturePython] Joint053  label="Distance048"  # Assembly joint (typed FeaturePython)
  Activated = true
  AngleMax = 0
  AngleMin = 0
  Detach1 = false
  Detach2 = false
  Distance = 0
  Distance2 = 0
  EnableAngleMax = false
  EnableAngleMin = false
  EnableLengthMax = false
  EnableLengthMin = false
  JointType = 5 (Distance)
  LengthMax = 0
  LengthMin = 0
  Placement1 = pos=(300,-7.5,1.137e-13) rot=(0,0,1;0rad)
  Placement2 = pos=(300,-1.137e-13,110) rot=(-0.57735,-0.57735,-0.57735;2.0944rad)
  Reference1 = -> Assembly [internal_separator_body.Face1,internal_separator_body.Face1]
  Reference2 = -> Assembly [internal_plate_body.Face5,internal_plate_body.Face5]
FEATURE [App::FeaturePython] Joint054  label="Distance049"  # Assembly joint (typed FeaturePython)
  Activated = true
  AngleMax = 0
  AngleMin = 0
  Detach1 = false
  Detach2 = false
  Distance = 0
  Distance2 = 0
  EnableAngleMax = false
  EnableAngleMin = false
  EnableLengthMax = false
  EnableLengthMin = false
  JointType = 5 (Distance)
  LengthMax = 0
  LengthMin = 0
  Placement1 = pos=(300,-15,250) rot=(-0.57735,-0.57735,-0.57735;2.0944rad)
  Placement2 = pos=(300,-7.5,220) rot=(0,-1,0;3.14159rad)
  Reference1 = -> Assembly [internal_separator_body.Face6,internal_separator_body.Face6]
  Reference2 = -> Assembly [internal_plate_body.Face3,internal_plate_body.Face3]
FEATURE [App::Link] side_body001  label="side_right"
  LinkPlacement = pos=(-2.336e-13,616,6.40146e-11) rot=(0,0,1;0rad)
  LinkedObject = -> <external side.FCStd>#Body
  Placement = pos=(-2.336e-13,616,6.40146e-11) rot=(0,0,1;0rad)
FEATURE [App::FeaturePython] Joint055  label="Distance050"  # Assembly joint (typed FeaturePython)
  Activated = true
  AngleMax = 0
  AngleMin = 0
  Detach1 = false
  Detach2 = false
  Distance = 0
  Distance2 = 0
  EnableAngleMax = false
  EnableAngleMin = false
  EnableLengthMax = false
  EnableLengthMin = false
  JointType = 5 (Distance)
  LengthMax = 0
  LengthMin = 0
  Placement1 = pos=(0,-8,782.322) rot=(0,-1,0;1.5708rad)
  Placement2 = pos=(0,-8,782.322) rot=(0,-1,0;1.5708rad)
  Reference1 = -> Assembly [side_body001.Face11,side_body001.Face11]
  Reference2 = -> Assembly [side_body.Face11,side_body.Face11]
FEATURE [App::FeaturePython] Joint056  label="Distance051"  # Assembly joint (typed FeaturePython)
  Activated = true
  AngleMax = 0
  AngleMin = 0
  Detach1 = false
  Detach2 = false
  Distance = 0
  Distance2 = 0
  EnableAngleMax = false
  EnableAngleMin = false
  EnableLengthMax = false
  EnableLengthMin = false
  JointType = 5 (Distance)
  LengthMax = 0
  LengthMin = 0
  Placement1 = pos=(225.638,-8,-8.278e-13) rot=(0,0,1;0rad)
  Placement2 = pos=(225.638,-8,-8.278e-13) rot=(0,0,1;0rad)
  Reference1 = -> Assembly [side_body001.Face7,side_body001.Face7]
  Reference2 = -> Assembly [side_body.Face7,side_body.Face7]
FEATURE [App::FeaturePython] Joint057  label="Distance052"  # Assembly joint (typed FeaturePython)
  Activated = true
  AngleMax = 0
  AngleMin = 0
  Detach1 = false
  Detach2 = false
  Distance = 0
  Distance2 = 0
  EnableAngleMax = false
  EnableAngleMin = false
  EnableLengthMax = false
  EnableLengthMin = false
  JointType = 5 (Distance)
  LengthMax = 0
  LengthMin = 0
  Placement1 = pos=(224.254,-16,770.624) rot=(-0.57735,-0.57735,-0.57735;2.0944rad)
  Placement2 = pos=(0,190,7.5) rot=(-0.57735,0.57735,-0.57735;2.0944rad)
  Reference1 = -> Assembly [side_body001.Face5,side_body001.Face5]
  Reference2 = -> Assembly [bottom_body.Face4,bottom_body.Face4]
FEATURE [App::Link] bottom_body001  label="subwoofer_top"
  LinkPlacement = pos=(17,-3.06703e-11,295) rot=(0.707107,0.707107,0;3.14159rad)
  LinkedObject = -> <external bottom.FCStd>#Body
  Placement = pos=(17,-3.06703e-11,295) rot=(0.707107,0.707107,0;3.14159rad)
FEATURE [App::FeaturePython] Joint058  label="Longueur"  # Assembly joint (typed FeaturePython)
  Activated = true
  AngleMax = 0
  AngleMin = 0
  Detach1 = false
  Detach2 = false
  Distance = 0
  Distance2 = 0
  EnableAngleMax = false
  EnableAngleMin = false
  EnableLengthMax = false
  EnableLengthMin = false
  JointType = 5 (Distance)
  LengthMax = 0
  LengthMin = 0
  Placement1 = pos=(224.254,-8.01027e-11,770.624) rot=(-0.57735,-0.57735,-0.57735;2.0944rad)
  Placement2 = pos=(0,190,7.5) rot=(-0.57735,0.57735,-0.57735;2.0944rad)
  Reference1 = -> Assembly [side_body.Fillet001.Face2,side_body.Fillet001.Face2]
  Reference2 = -> Assembly [bottom_body001.Pad.Face4,bottom_body001.Pad.Face4]
FEATURE [App::FeaturePython] Joint059  label="Longueur001"  # Assembly joint (typed FeaturePython)
  Activated = true
  AngleMax = 0
  AngleMin = 0
  Detach1 = false
  Detach2 = false
  Distance = 0
  Distance2 = 0
  EnableAngleMax = false
  EnableAngleMin = false
  EnableLengthMax = false
  EnableLengthMin = false
  JointType = 5 (Distance)
  LengthMax = 0
  LengthMin = 0
  Placement1 = pos=(300,190,0) rot=(0,0,1;0rad)
  Placement2 = pos=(300,-7.5,500) rot=(0,-1,0;3.14159rad)
  Reference1 = -> Assembly [bottom_body001.Pad.Face5,bottom_body001.Pad.Face5]
  Reference2 = -> Assembly [internal_separator_body.Pad.Face3,internal_separator_body.Pad.Face3]
FEATURE [App::FeaturePython] Joint060  label="Longueur002"  # Assembly joint (typed FeaturePython)
  Activated = true
  AngleMax = 0
  AngleMin = 0
  Detach1 = false
  Detach2 = false
  Distance = 0
  Distance2 = 0
  EnableAngleMax = false
  EnableAngleMin = false
  EnableLengthMax = false
  EnableLengthMin = false
  JointType = 5 (Distance)
  LengthMax = 0
  LengthMin = 0
  Placement1 = pos=(300,380,7.5) rot=(0,-0.707107,0.707107;3.14159rad)
  Placement2 = pos=(15,300,425) rot=(0.707107,0,0.707107;3.14159rad)
  Reference1 = -> Assembly [bottom_body001.Pad.Face3,bottom_body001.Pad.Face3]
  Reference2 = -> Assembly [front_body.Pad.Face6,front_body.Pad.Face6]
FEATURE [Assembly::JointGroup] Joints
  Group = -> [GroundedJoint,Joint,Joint001,Joint002,Joint003,Joint004,Joint005,Joint006,Joint007,Joint008,Joint009,Joint010,Joint011,Joint012,Joint013,Joint014,Joint015,Joint016,Joint017,Joint019,Joint020,Joint021,Joint022,Joint023,Joint024,Joint025,Joint026,Joint027,Joint028,Joint029,Joint030,Joint031,Joint032,Joint033,Joint034,Joint035,Joint036,Joint037,Joint039,Joint040,Joint041,Joint042,Joint043,Joint044,+16 more]
FEATURE [Assembly::AssemblyObject] Assembly
  Group = -> [Joints,bottom_body,side_body,speaker_panel_body,top_body,marquee_body,Body,front_body,fan_plane_body,ctrl_panel_body,ctrl_panel_body001,Body001,connector_panel_body,GroundedJoint,Joint,Joint001,Joint002,Joint003,Joint004,Joint005,Joint006,Joint007,Joint008,Joint009,Joint010,Joint011,Joint012,Joint013,Joint014,Joint015,Joint016,Joint017,Joint019,Joint020,Joint021,Joint022,Joint023,Joint024,+42 more]
  Origin = -> Origin
  Type = Assembly

RESOLVED EXTERNAL PARTS (link-assembly join: the EXTERNAL_REF files above that resolve inside this repo's crawl, each included once):
---- part back_bottom.FCStd = doc fcstd_d52e2de3eea4 ----
FCSTD DOCUMENT  (FreeCAD 1.0R39319 (Git))
Label: back_bottom
License: All rights reserved
LicenseURL: https://en.wikipedia.org/wiki/All_rights_reserved
objects: Sketcher::SketchObject×1, PartDesign::Pad×1, PartDesign::Body×1
note: 6 computed .brp shape members not serialized (recipe doc carries the construction recipe); baked Part::Feature solids carry a one-line shape summary decoded from their .brp

FEATURE [Sketcher::SketchObject] Sketch  label="back_bottom_s"
  ArcFitTolerance = 1e-06
  AttachmentSupport = -> [XZ_Plane]
  FullyConstrained = true
  MakeInternals = false
  MapMode = 5
  Placement = pos=(0,0,0) rot=(1,0,0;1.5708rad)
  sketch-geometry (4):
    g0: LineSegment StartX=0 StartY=0 StartZ=0 EndX=600 EndY=0 EndZ=0
    g1: LineSegment StartX=600 StartY=0 StartZ=0 EndX=600 EndY=290 EndZ=0
    g2: LineSegment StartX=600 StartY=290 StartZ=0 EndX=0 EndY=290 EndZ=0
    g3: LineSegment StartX=0 StartY=290 StartZ=0 EndX=0 EndY=0 EndZ=0
  constraints (11):
    c: Coincident(g0,g1)
    c: Coincident(g1,g2)
    c: Coincident(g2,g3)
    c: Coincident(g3,g0)
    c: Horizontal(g0)
    c: Horizontal(g2)
    c: Vertical(g1)
    c: Vertical(g3)
    c: Coincident(g0,g-1)
    c: DistanceX(g2,g2) = 600
    c: DistanceY(g3,g3) = 290
FEATURE [PartDesign::Pad] Pad  label="back_bottom"
  Direction = (0,-1,2e-16)
  Length = 15
  Length2 = 10
  Placement = pos=(0,0,0) rot=(1,0,0;1.5708rad)
  Profile = -> Sketch
  ReferenceAxis = -> Sketch [N_Axis]
  Refine = true
  Suppressed = false
  Type = 0
FEATURE [PartDesign::Body] Body  label="back_bottom_body"
  AllowCompound = false
  Group = -> [Sketch,Pad]
  Origin = -> Origin
  Tip = -> Pad
---- part back_bottom_door.FCStd = doc fcstd_a515aa9ce11e ----
FCSTD DOCUMENT  (FreeCAD 1.0R39319 (Git))
Label: back_bottom_door
License: All rights reserved
LicenseURL: https://en.wikipedia.org/wiki/All_rights_reserved
objects: Sketcher::SketchObject×1, PartDesign::Pad×1, PartDesign::Body×1
note: 6 computed .brp shape members not serialized (recipe doc carries the construction recipe); baked Part::Feature solids carry a one-line shape summary decoded from their .brp

FEATURE [Sketcher::SketchObject] Sketch  label="back_bottom_door_s"
  ArcFitTolerance = 1e-06
  AttachmentSupport = -> [XZ_Plane]
  FullyConstrained = true
  MakeInternals = false
  MapMode = 5
  Placement = pos=(0,0,0) rot=(1,0,0;1.5708rad)
  sketch-geometry (4):
    g0: LineSegment StartX=0 StartY=0 StartZ=0 EndX=600 EndY=0 EndZ=0
    g1: LineSegment StartX=600 StartY=0 StartZ=0 EndX=600 EndY=430 EndZ=0
    g2: LineSegment StartX=600 StartY=430 StartZ=0 EndX=0 EndY=430 EndZ=0
    g3: LineSegment StartX=0 StartY=430 StartZ=0 EndX=0 EndY=0 EndZ=0
  constraints (11):
    c: Coincident(g0,g1)
    c: Coincident(g1,g2)
    c: Coincident(g2,g3)
    c: Coincident(g3,g0)
    c: Horizontal(g0)
    c: Horizontal(g2)
    c: Vertical(g1)
    c: Vertical(g3)
    c: Coincident(g0,g-1)
    c: DistanceX(g2,g2) = 600
    c: DistanceY(g3,g3) = 430
FEATURE [PartDesign::Pad] Pad  label="back_bottom_door"
  Direction = (0,-1,2e-16)
  Length = 15
  Length2 = 10
  Placement = pos=(0,0,0) rot=(1,0,0;1.5708rad)
  Profile = -> Sketch
  ReferenceAxis = -> Sketch [N_Axis]
  Refine = true
  Suppressed = false
  Type = 0
FEATURE [PartDesign::Body] Body  label="back_bottom_door_body"
  AllowCompound = false
  Group = -> [Sketch,Pad]
  Origin = -> Origin
  Tip = -> Pad
---- part back_top_door.FCStd = doc fcstd_c87b5e8a9fea ----
FCSTD DOCUMENT  (FreeCAD 1.0R39319 (Git))
Label: back_top_door
License: All rights reserved
LicenseURL: https://en.wikipedia.org/wiki/All_rights_reserved
objects: Sketcher::SketchObject×1, PartDesign::Pad×1, PartDesign::Body×1
note: 6 computed .brp shape members not serialized (recipe doc carries the construction recipe); baked Part::Feature solids carry a one-line shape summary decoded from their .brp

FEATURE [Sketcher::SketchObject] Sketch  label="back_top_door_s"
  ArcFitTolerance = 1e-06
  AttachmentSupport = -> [XZ_Plane]
  FullyConstrained = true
  MakeInternals = false
  MapMode = 5
  Placement = pos=(0,0,0) rot=(1,0,0;1.5708rad)
  sketch-geometry (4):
    g0: LineSegment StartX=0 StartY=0 StartZ=0 EndX=600 EndY=0 EndZ=0
    g1: LineSegment StartX=600 StartY=0 StartZ=0 EndX=600 EndY=460 EndZ=0
    g2: LineSegment StartX=600 StartY=460 StartZ=0 EndX=0 EndY=460 EndZ=0
    g3: LineSegment StartX=0 StartY=460 StartZ=0 EndX=0 EndY=0 EndZ=0
  constraints (11):
    c: Coincident(g0,g1)
    c: Coincident(g1,g2)
    c: Coincident(g2,g3)
    c: Coincident(g3,g0)
    c: Horizontal(g0)
    c: Horizontal(g2)
    c: Vertical(g1)
    c: Vertical(g3)
    c: Coincident(g0,g-1)
    c: DistanceX(g2,g2) = 600
    c: DistanceY(g3,g3) = 460
FEATURE [PartDesign::Pad] Pad  label="back_top_door"
  Direction = (0,-1,2e-16)
  Length = 15
  Length2 = 10
  Placement = pos=(0,0,0) rot=(1,0,0;1.5708rad)
  Profile = -> Sketch
  ReferenceAxis = -> Sketch [N_Axis]
  Refine = true
  Suppressed = false
  Type = 0
FEATURE [PartDesign::Body] Body  label="back_top_door_body"
  AllowCompound = false
  Group = -> [Sketch,Pad]
  Origin = -> Origin
  Tip = -> Pad
---- part bottom.FCStd = doc fcstd_0f6f75d44551 ----
FCSTD DOCUMENT  (FreeCAD 1.0R39319 (Git))
Label: bottom
License: All rights reserved
LicenseURL: http://en.wikipedia.org/wiki/All_rights_reserved
objects: Sketcher::SketchObject×1, PartDesign::Pad×1, PartDesign::Body×1
note: 6 computed .brp shape members not serialized (recipe doc carries the construction recipe); baked Part::Feature solids carry a one-line shape summary decoded from their .brp

FEATURE [Sketcher::SketchObject] Sketch  label="bottom_sketch"
  ArcFitTolerance = 0
  AttachmentSupport = -> [XY_Plane]
  FullyConstrained = true
  MakeInternals = false
  MapMode = 5
  sketch-geometry (4):
    g0: LineSegment StartX=0 StartY=0 StartZ=0 EndX=600 EndY=0 EndZ=0
    g1: LineSegment StartX=600 StartY=0 StartZ=0 EndX=600 EndY=380 EndZ=0
    g2: LineSegment StartX=600 StartY=380 StartZ=0 EndX=0 EndY=380 EndZ=0
    g3: LineSegment StartX=0 StartY=380 StartZ=0 EndX=0 EndY=0 EndZ=0
  constraints (11):
    c: Coincident(g0,g1)
    c: Coincident(g1,g2)
    c: Coincident(g2,g3)
    c: Coincident(g3,g0)
    c: Horizontal(g0)
    c: Horizontal(g2)
    c: Vertical(g1)
    c: Vertical(g3)
    c: Coincident(g0,g-1)
    c: DistanceX(g0,g0) = 600
    c: DistanceY(g3,g3) = 380
FEATURE [PartDesign::Pad] Pad  label="bottom_pad"
  AllowMultiFace = false
  Direction = (0,0,1)
  Length = 15
  Length2 = 100
  Profile = -> Sketch
  ReferenceAxis = -> Sketch [N_Axis]
  Suppressed = false
  Type = 0
FEATURE [PartDesign::Body] Body  label="bottom_body"
  AllowCompound = false
  Group = -> [Sketch,Pad]
  Origin = -> Origin
  Tip = -> Pad
---- part connector_panel.FCStd = doc fcstd_88cc0b0be0d1 ----
FCSTD DOCUMENT  (FreeCAD 1.0R39319 (Git))
Label: connector_panel
License: All rights reserved
LicenseURL: http://en.wikipedia.org/wiki/All_rights_reserved
objects: Sketcher::SketchObject×1, PartDesign::Pad×1, PartDesign::Body×1
note: 6 computed .brp shape members not serialized (recipe doc carries the construction recipe); baked Part::Feature solids carry a one-line shape summary decoded from their .brp

FEATURE [Sketcher::SketchObject] Sketch  label="connector_panel_sketch"
  ArcFitTolerance = 0
  AttachmentSupport = -> [YZ_Plane]
  FullyConstrained = true
  MakeInternals = false
  MapMode = 5
  Placement = pos=(0,0,0) rot=(0.57735,0.57735,0.57735;2.0944rad)
  sketch-geometry (21):
    g0: LineSegment StartX=0 StartY=0 StartZ=0 EndX=600 EndY=0 EndZ=0
    g1: LineSegment StartX=600 StartY=0 StartZ=0 EndX=600 EndY=300 EndZ=0
    g2: LineSegment StartX=600 StartY=300 StartZ=0 EndX=0 EndY=300 EndZ=0
    g3: LineSegment StartX=0 StartY=300 StartZ=0 EndX=0 EndY=0 EndZ=0
    g4: LineSegment StartX=40 StartY=174 StartZ=0 EndX=68 EndY=174 EndZ=0
    g5: LineSegment StartX=68 StartY=174 StartZ=0 EndX=68 EndY=126 EndZ=0
    g6: LineSegment StartX=68 StartY=126 StartZ=0 EndX=40 EndY=126 EndZ=0
    g7: LineSegment StartX=40 StartY=126 StartZ=0 EndX=40 EndY=174 EndZ=0
    g8: Circle CenterX=200 CenterY=40 CenterZ=0 NormalX=0 NormalY=0 NormalZ=1 AngleXU=0 Radius=12
    g9: Circle CenterX=266.667 CenterY=40 CenterZ=0 NormalX=0 NormalY=0 NormalZ=1 AngleXU=0 Radius=12
    g10: Circle CenterX=333.333 CenterY=40 CenterZ=0 NormalX=0 NormalY=0 NormalZ=1 AngleXU=0 Radius=12
    g11: Circle CenterX=400 CenterY=40 CenterZ=0 NormalX=0 NormalY=0 NormalZ=1 AngleXU=0 Radius=12
    g12: LineSegment [constr] StartX=40 StartY=126 StartZ=0 EndX=0 EndY=126 EndZ=0
    g13: LineSegment [constr] StartX=200 StartY=40 StartZ=0 EndX=266.667 EndY=40 EndZ=0
    g14: LineSegment [constr] StartX=333.333 StartY=40 StartZ=0 EndX=400 EndY=40 EndZ=0
    g15: LineSegment [constr] StartX=40 StartY=126 StartZ=0 EndX=40 EndY=0 EndZ=0
    g16: LineSegment [constr] StartX=40 StartY=174 StartZ=0 EndX=40 EndY=300 EndZ=0
    g17: LineSegment [constr] StartX=200 StartY=40 StartZ=0 EndX=200 EndY=0 EndZ=0
    g18: LineSegment [constr] StartX=266.667 StartY=40 StartZ=0 EndX=333.333 EndY=40 EndZ=0
    g19: LineSegment [constr] StartX=200 StartY=40 StartZ=0 EndX=0 EndY=40 EndZ=0
    g20: LineSegment [constr] StartX=400 StartY=40 StartZ=0 EndX=600 EndY=40 EndZ=0
  constraints (59):
    c: Coincident(g0,g1)
    c: Coincident(g1,g2)
    c: Coincident(g2,g3)
    c: Coincident(g3,g0)
    c: Horizontal(g0)
    c: Horizontal(g2)
    c: Vertical(g1)
    c: Vertical(g3)
    c: Coincident(g0,g-1)
    c: DistanceY(g3,g3) = 300
    c: DistanceX(g0,g0) = 600
    c: Coincident(g4,g5)
    c: Coincident(g5,g6)
    c: Coincident(g6,g7)
    c: Coincident(g7,g4)
    c: Horizontal(g4)
    c: Horizontal(g6)
    c: Vertical(g5)
    c: Vertical(g7)
    c: DistanceX(g4,g4) = 28
    c: DistanceY(g7,g7) = 48
    c: Radius(g8) = 12
    c: Radius(g9) = 12
    c: Radius(g10) = 12
    c: Radius(g11) = 12
    c: Coincident(g12,g6)
    c: PointOnObject(g12,g3)
    c: Horizontal(g12)
    c: Coincident(g13,g8)
    c: Coincident(g13,g9)
    c: Horizontal(g13)
    c: Coincident(g14,g10)
    c: Coincident(g14,g11)
    c: Horizontal(g14)
    c: Equal(g13,g14)
    c: Coincident(g15,g6)
    c: PointOnObject(g15,g0)
    c: Vertical(g15)
    c: Coincident(g16,g4)
    c: PointOnObject(g16,g2)
    c: Vertical(g16)
    c: Equal(g16,g15)
    c: DistanceX(g12,g12) = 40
    c: Coincident(g17,g8)
    c: PointOnObject(g17,g0)
    c: Vertical(g17)
    c: DistanceX(g-1,g17) = 200
    c: Coincident(g18,g9)
    c: Coincident(g18,g10)
    c: Horizontal(g18)
    c: Equal(g18,g14)
    c: DistanceY(g17,g17) = 40
    c: Coincident(g19,g8)
    c: PointOnObject(g19,g3)
    c: Horizontal(g19)
    c: Coincident(g20,g11)
    c: PointOnObject(g20,g1)
    c: Horizontal(g20)
    c: Equal(g19,g20)
FEATURE [PartDesign::Pad] Pad  label="connector_panel_pad"
  AllowMultiFace = false
  Direction = (1,-1.129e-13,1.129e-13)
  Length = 15
  Length2 = 100
  Placement = pos=(0,0,0) rot=(0.57735,0.57735,0.57735;2.0944rad)
  Profile = -> Sketch
  ReferenceAxis = -> Sketch [N_Axis]
  Suppressed = false
  Type = 0
FEATURE [PartDesign::Body] Body  label="connector_panel_body"
  AllowCompound = false
  Group = -> [Sketch,Pad]
  Origin = -> Origin
  Tip = -> Pad
---- part control_panel.FCStd = doc fcstd_31da0969b1f1 ----
FCSTD DOCUMENT  (FreeCAD 1.0R39319 (Git))
Label: control_panel
License: All rights reserved
LicenseURL: http://fr.wikipedia.org/wiki/<copyright redacted>
objects: Sketcher::SketchObject×1, PartDesign::Pad×1, PartDesign::Body×1
note: 6 computed .brp shape members not serialized (recipe doc carries the construction recipe); baked Part::Feature solids carry a one-line shape summary decoded from their .brp

FEATURE [Sketcher::SketchObject] Sketch  label="control_panel_sketch"
  ArcFitTolerance = 0
  AttachmentSupport = -> [XY_Plane]
  FullyConstrained = true
  MakeInternals = false
  MapMode = 5
  sketch-geometry (23):
    g0: Circle CenterX=70 CenterY=100 CenterZ=0 NormalX=0 NormalY=0 NormalZ=1 AngleXU=0 Radius=12
    g1: Circle CenterX=129 CenterY=85.1 CenterZ=0 NormalX=0 NormalY=0 NormalZ=1 AngleXU=0 Radius=15
    g2: Circle CenterX=164 CenterY=100 CenterZ=0 NormalX=0 NormalY=0 NormalZ=1 AngleXU=0 Radius=15
    g3: Circle CenterX=202.2 CenterY=93.6 CenterZ=0 NormalX=0 NormalY=0 NormalZ=1 AngleXU=0 Radius=15
    g4: Circle CenterX=171 CenterY=140.9 CenterZ=0 NormalX=0 NormalY=0 NormalZ=1 AngleXU=0 Radius=15
    g5: Circle CenterX=209.2 CenterY=134.5 CenterZ=0 NormalX=0 NormalY=0 NormalZ=1 AngleXU=0 Radius=15
    g6: Circle CenterX=136 CenterY=126 CenterZ=0 NormalX=0 NormalY=0 NormalZ=1 AngleXU=0 Radius=15
    g7: LineSegment [constr] StartX=171 StartY=140.9 StartZ=0 EndX=209.2 EndY=134.5 EndZ=0
    g8: LineSegment [constr] StartX=202.2 StartY=93.6 StartZ=0 EndX=164 EndY=100 EndZ=0
    g9: LineSegment StartX=0 StartY=0 StartZ=0 EndX=600 EndY=0 EndZ=0
    g10: LineSegment StartX=600 StartY=0 StartZ=0 EndX=600 EndY=200 EndZ=0
    g11: LineSegment StartX=600 StartY=200 StartZ=0 EndX=0 EndY=200 EndZ=0
    g12: LineSegment StartX=0 StartY=200 StartZ=0 EndX=0 EndY=0 EndZ=0
    g13: Circle CenterX=390.8 CenterY=100 CenterZ=0 NormalX=0 NormalY=0 NormalZ=1 AngleXU=0 Radius=12
    g14: Circle CenterX=449.8 CenterY=85.1 CenterZ=0 NormalX=0 NormalY=0 NormalZ=1 AngleXU=0 Radius=15
    g15: Circle CenterX=484.8 CenterY=100 CenterZ=0 NormalX=0 NormalY=0 NormalZ=1 AngleXU=0 Radius=15
    g16: Circle CenterX=523 CenterY=93.6 CenterZ=0 NormalX=0 NormalY=0 NormalZ=1 AngleXU=0 Radius=15
    g17: Circle CenterX=491.8 CenterY=140.9 CenterZ=0 NormalX=0 NormalY=0 NormalZ=1 AngleXU=0 Radius=15
    g18: Circle CenterX=530 CenterY=134.5 CenterZ=0 NormalX=0 NormalY=0 NormalZ=1 AngleXU=0 Radius=15
    g19: Circle CenterX=456.8 CenterY=126 CenterZ=0 NormalX=0 NormalY=0 NormalZ=1 AngleXU=0 Radius=15
    g20: LineSegment [constr] StartX=491.8 StartY=140.9 StartZ=0 EndX=530 EndY=134.5 EndZ=0
    g21: LineSegment [constr] StartX=523 StartY=93.6 StartZ=0 EndX=484.8 EndY=100 EndZ=0
    g22: LineSegment [constr] StartX=70 StartY=100 StartZ=0 EndX=390.8 EndY=100 EndZ=0
  constraints (63):
    c: Radius(g0) = 12
    c: Radius(g6) = 15
    c: Equal(g6,g4)
    c: Equal(g4,g5)
    c: Equal(g5,g2)
    c: Equal(g2,g3)
    c: Equal(g1,g6)
    c: DistanceX(g0,g1) = 59
    c: DistanceX(g6,g4) = 35
    c: DistanceX(g4,g5) = 38.2
    c: DistanceX(g1,g2) = 35
    c: DistanceX(g2,g3) = 38.2
    c: DistanceX(g0,g6) = 66
    c: DistanceY(g1,g0) = 14.9
    c: DistanceY(g0,g6) = 26
    c: DistanceY(g1,g2) = 14.9
    c: DistanceY(g3,g2) = 6.4
    c: DistanceY(g6,g4) = 14.9
    c: DistanceY(g5,g4) = 6.4
    c: Coincident(g7,g4)
    c: Coincident(g8,g2)
    c: Coincident(g9,g10)
    c: Coincident(g10,g11)
    c: Coincident(g11,g12)
    c: Coincident(g12,g9)
    c: Horizontal(g9)
    c: Horizontal(g11)
    c: Vertical(g10)
    c: Vertical(g12)
    c: Coincident(g9,g-1)
    c: DistanceX(g9,g9) = 600
    c: Equal(g0,g13) = 14
    c: Equal(g6,g19) = 15
    c: Equal(g19,g17)
    c: Equal(g17,g18)
    c: Equal(g18,g15)
    c: Equal(g15,g16)
    c: Equal(g14,g19)
    c: DistanceX(g13,g14) = 59
    c: DistanceX(g19,g17) = 35
    c: DistanceX(g17,g18) = 38.2
    c: DistanceX(g14,g15) = 35
    c: DistanceX(g15,g16) = 38.2
    c: DistanceX(g13,g19) = 66
    c: DistanceY(g14,g13) = 14.9
    c: DistanceY(g13,g19) = 26
    c: DistanceY(g14,g15) = 14.9
    c: DistanceY(g16,g15) = 6.4
    c: DistanceY(g19,g17) = 14.9
    c: DistanceY(g18,g17) = 6.4
    c: Coincident(g20,g17)
    c: Coincident(g21,g15)
    c: DistanceX(g-1,g0) = 70
    c: DistanceY(g12,g12) = 200
    c: DistanceY(g-1,g0) = 100
    c: Coincident(g22,g0)
    c: Coincident(g22,g13)
    c: Horizontal(g22)
    c: Coincident(g21,g16)
    c: Coincident(g20,g18)
    c: Coincident(g8,g3)
    c: Coincident(g7,g5)
    c: DistanceX(g18,g10) = 70
FEATURE [PartDesign::Pad] Pad
  AllowMultiFace = false
  Direction = (0,0,1)
  Length = 15
  Length2 = 100
  Profile = -> Sketch
  ReferenceAxis = -> Sketch [N_Axis]
  Suppressed = false
  Type = 0
FEATURE [PartDesign::Body] Body
  AllowCompound = false
  Group = -> [Sketch,Pad]
  Origin = -> Origin
  Tip = -> Pad
---- part ctrl_panel_bottom.FCStd = doc fcstd_645d12bdc173 ----
FCSTD DOCUMENT  (FreeCAD 1.0R39319 (Git))
Label: ctrl_panel_bottom
License: All rights reserved
LicenseURL: http://en.wikipedia.org/wiki/All_rights_reserved
objects: Sketcher::SketchObject×1, PartDesign::Pad×1, PartDesign::Body×1
note: 6 computed .brp shape members not serialized (recipe doc carries the construction recipe); baked Part::Feature solids carry a one-line shape summary decoded from their .brp

FEATURE [Sketcher::SketchObject] Sketch  label="ctrl_panel_bottom_sketch"
  ArcFitTolerance = 0
  AttachmentSupport = -> [XY_Plane]
  FullyConstrained = true
  MakeInternals = false
  MapMode = 5
  sketch-geometry (10):
    g0: LineSegment StartX=0 StartY=0 StartZ=0 EndX=600 EndY=0 EndZ=0
    g1: LineSegment StartX=600 StartY=0 StartZ=0 EndX=600 EndY=140 EndZ=0
    g2: LineSegment StartX=600 StartY=140 StartZ=0 EndX=0 EndY=140 EndZ=0
    g3: LineSegment StartX=0 StartY=140 StartZ=0 EndX=0 EndY=0 EndZ=0
    g4: Circle CenterX=40 CenterY=90 CenterZ=0 NormalX=0 NormalY=0 NormalZ=1 AngleXU=0 Radius=12
    g5: Circle CenterX=560 CenterY=90 CenterZ=0 NormalX=0 NormalY=0 NormalZ=1 AngleXU=0 Radius=12
    g6: LineSegment [constr] StartX=40 StartY=90 StartZ=0 EndX=0 EndY=90 EndZ=0
    g7: LineSegment [constr] StartX=40 StartY=90 StartZ=0 EndX=40 EndY=140 EndZ=0
    g8: LineSegment [constr] StartX=560 StartY=90 StartZ=0 EndX=560 EndY=140 EndZ=0
    g9: LineSegment [constr] StartX=560 StartY=90 StartZ=0 EndX=600 EndY=90 EndZ=0
  constraints (29):
    c: Coincident(g0,g1)
    c: Coincident(g1,g2)
    c: Coincident(g2,g3)
    c: Coincident(g3,g0)
    c: Horizontal(g0)
    c: Horizontal(g2)
    c: Vertical(g1)
    c: Vertical(g3)
    c: Coincident(g0,g-1)
    c: DistanceX(g0,g0) = 600
    c: DistanceY(g3,g3) = 140
    c: Radius(g4) = 12
    c: Radius(g5) = 12
    c: Coincident(g6,g4)
    c: PointOnObject(g6,g3)
    c: Horizontal(g6)
    c: PointOnObject(g7,g2)
    c: Vertical(g7)
    c: Coincident(g8,g5)
    c: PointOnObject(g8,g2)
    c: Vertical(g8)
    c: Coincident(g9,g5)
    c: PointOnObject(g9,g1)
    c: Horizontal(g9)
    c: Equal(g6,g9)
    c: Equal(g8,g7)
    c: DistanceY(g7,g7) = 50
    c: Coincident(g7,g4)
    c: DistanceX(g6,g6) = 40
FEATURE [PartDesign::Pad] Pad  label="ctrl_panel_pad"
  AllowMultiFace = false
  Direction = (0,0,1)
  Length = 15
  Length2 = 100
  Profile = -> Sketch
  ReferenceAxis = -> Sketch [N_Axis]
  Suppressed = false
  Type = 0
FEATURE [PartDesign::Body] Body  label="ctrl_panel_body"
  AllowCompound = false
  Group = -> [Sketch,Pad]
  Origin = -> Origin
  Tip = -> Pad
---- part ctrl_panel_front.FCStd = doc fcstd_85dac185042a ----
FCSTD DOCUMENT  (FreeCAD 1.0R39319 (Git))
Label: ctrl_panel_front
License: All rights reserved
LicenseURL: http://en.wikipedia.org/wiki/All_rights_reserved
objects: Sketcher::SketchObject×1, PartDesign::Pad×1, PartDesign::Body×1
note: 6 computed .brp shape members not serialized (recipe doc carries the construction recipe); baked Part::Feature solids carry a one-line shape summary decoded from their .brp

FEATURE [Sketcher::SketchObject] Sketch  label="ctrl_panel_front_sketch"
  ArcFitTolerance = 0
  AttachmentSupport = -> [XY_Plane]
  FullyConstrained = true
  MakeInternals = false
  MapMode = 5
  sketch-geometry (23):
    g0: LineSegment StartX=0 StartY=0 StartZ=0 EndX=600 EndY=0 EndZ=0
    g1: LineSegment StartX=600 StartY=0 StartZ=0 EndX=600 EndY=120 EndZ=0
    g2: LineSegment StartX=600 StartY=120 StartZ=0 EndX=0 EndY=120 EndZ=0
    g3: LineSegment StartX=0 StartY=120 StartZ=0 EndX=0 EndY=0 EndZ=0
    g4: Circle CenterX=80 CenterY=70 CenterZ=0 NormalX=0 NormalY=0 NormalZ=1 AngleXU=0 Radius=14
    g5: Circle CenterX=450 CenterY=70 CenterZ=0 NormalX=0 NormalY=0 NormalZ=1 AngleXU=0 Radius=14
    g6: LineSegment [constr] StartX=80 StartY=70 StartZ=0 EndX=0 EndY=70 EndZ=0
    g7: LineSegment [constr] StartX=80 StartY=70 StartZ=0 EndX=80 EndY=120 EndZ=0
    g8: LineSegment [constr] StartX=450 StartY=70 StartZ=0 EndX=450 EndY=120 EndZ=0
    g9: LineSegment StartX=133 StartY=87 StartZ=0 EndX=133 EndY=53 EndZ=0
    g10: LineSegment StartX=133 StartY=53 StartZ=0 EndX=167 EndY=53 EndZ=0
    g11: LineSegment StartX=167 StartY=53 StartZ=0 EndX=167 EndY=87 EndZ=0
    g12: LineSegment StartX=167 StartY=87 StartZ=0 EndX=133 EndY=87 EndZ=0
    g13: LineSegment [constr] StartX=133 StartY=87 StartZ=0 EndX=167 EndY=53 EndZ=0
    g14: LineSegment [constr] StartX=167 StartY=87 StartZ=0 EndX=133 EndY=53 EndZ=0
    g15: GeomPoint [constr] X=150 Y=70 Z=0
    g16: LineSegment StartX=503 StartY=87 StartZ=0 EndX=503 EndY=53 EndZ=0
    g17: LineSegment StartX=503 StartY=53 StartZ=0 EndX=537 EndY=53 EndZ=0
    g18: LineSegment StartX=537 StartY=53 StartZ=0 EndX=537 EndY=87 EndZ=0
    g19: LineSegment StartX=537 StartY=87 StartZ=0 EndX=503 EndY=87 EndZ=0
    g20: LineSegment [constr] StartX=503 StartY=53 StartZ=0 EndX=537 EndY=87 EndZ=0
    g21: LineSegment [constr] StartX=537 StartY=53 StartZ=0 EndX=503 EndY=87 EndZ=0
    g22: GeomPoint [constr] X=520 Y=70 Z=0
  constraints (62):
    c: Coincident(g0,g1)
    c: Coincident(g1,g2)
    c: Coincident(g2,g3)
    c: Coincident(g3,g0)
    c: Horizontal(g0)
    c: Horizontal(g2)
    c: Vertical(g1)
    c: Vertical(g3)
    c: Coincident(g0,g-1)
    c: DistanceX(g0,g0) = 600
    c: DistanceY(g3,g3) = 120
    c: Coincident(g6,g4)
    c: PointOnObject(g6,g3)
    c: Horizontal(g6)
    c: PointOnObject(g7,g2)
    c: Vertical(g7)
    c: Coincident(g8,g5)
    c: PointOnObject(g8,g2)
    c: Vertical(g8)
    c: Equal(g8,g7)
    c: DistanceY(g7,g7) = 50
    c: Coincident(g7,g4)
    c: DistanceX(g6,g6) = 80
    c: DistanceX(g5,g1) = 150
    c: Diameter(g4) = 28
    c: Equal(g5,g4)
    c: Coincident(g9,g10)
    c: Coincident(g10,g11)
    c: Coincident(g11,g12)
    c: Coincident(g12,g9)
    c: Vertical(g9)
    c: Vertical(g11)
    c: Horizontal(g10)
    c: Horizontal(g12)
    c: Equal(g10,g11)
    c: DistanceX(g12,g12) = 34
    c: Coincident(g13,g9)
    c: Coincident(g13,g10)
    c: Coincident(g14,g11)
    c: Coincident(g14,g9)
    c: PointOnObject(g15,g14)
    c: PointOnObject(g15,g13)
    c: DistanceX(g2,g15) = 150
    c: PointOnObject(g15,g6)
    c: Coincident(g16,g17)
    c: Coincident(g17,g18)
    c: Coincident(g18,g19)
    c: Coincident(g19,g16)
    c: Vertical(g16)
    c: Vertical(g18)
    c: Horizontal(g17)
    c: Horizontal(g19)
    c: Equal(g17,g16)
    c: Equal(g16,g11)
    c: PointOnObject(g16,g12)
    c: Coincident(g20,g16)
    c: Coincident(g20,g18)
    c: Coincident(g21,g17)
    c: Coincident(g21,g16)
    c: PointOnObject(g22,g20)
    c: PointOnObject(g22,g21)
    c: DistanceX(g22,g1) = 80
FEATURE [PartDesign::Pad] Pad  label="ctrl_panel_pad"
  AllowMultiFace = false
  Direction = (0,0,1)
  Length = 15
  Length2 = 100
  Profile = -> Sketch
  ReferenceAxis = -> Sketch [N_Axis]
  Suppressed = false
  Type = 0
FEATURE [PartDesign::Body] Body  label="ctrl_panel_body"
  AllowCompound = false
  Group = -> [Sketch,Pad]
  Origin = -> Origin
  Tip = -> Pad
---- part fan_plane.FCStd = doc fcstd_905c31174287 ----
FCSTD DOCUMENT  (FreeCAD 1.0R39319 (Git))
Label: fan_plane
License: All rights reserved
LicenseURL: http://en.wikipedia.org/wiki/All_rights_reserved
objects: Sketcher::SketchObject×1, PartDesign::Pad×1, PartDesign::Body×1
note: 6 computed .brp shape members not serialized (recipe doc carries the construction recipe); baked Part::Feature solids carry a one-line shape summary decoded from their .brp

FEATURE [Sketcher::SketchObject] Sketch  label="fan_plane_sketch"
  ArcFitTolerance = 0
  AttachmentSupport = -> [XY_Plane]
  FullyConstrained = true
  MakeInternals = false
  MapMode = 5
  sketch-geometry (10):
    g0: LineSegment StartX=0 StartY=0 StartZ=0 EndX=600 EndY=0 EndZ=0
    g1: LineSegment StartX=600 StartY=0 StartZ=0 EndX=600 EndY=180 EndZ=0
    g2: LineSegment StartX=600 StartY=180 StartZ=0 EndX=0 EndY=180 EndZ=0
    g3: LineSegment StartX=0 StartY=180 StartZ=0 EndX=0 EndY=0 EndZ=0
    g4: Circle CenterX=120 CenterY=90 CenterZ=0 NormalX=0 NormalY=0 NormalZ=1 AngleXU=0 Radius=60
    g5: Circle CenterX=480 CenterY=90 CenterZ=0 NormalX=0 NormalY=0 NormalZ=1 AngleXU=0 Radius=60
    g6: LineSegment [constr] StartX=120 StartY=90 StartZ=0 EndX=0 EndY=90 EndZ=0
    g7: LineSegment [constr] StartX=480 StartY=90 StartZ=0 EndX=600 EndY=90 EndZ=0
    g8: LineSegment [constr] StartX=480 StartY=90 StartZ=0 EndX=480 EndY=0 EndZ=0
    g9: LineSegment [constr] StartX=120 StartY=90 StartZ=0 EndX=120 EndY=180 EndZ=0
  constraints (29):
    c: Coincident(g0,g1)
    c: Coincident(g1,g2)
    c: Coincident(g2,g3)
    c: Coincident(g3,g0)
    c: Horizontal(g0)
    c: Horizontal(g2)
    c: Vertical(g1)
    c: Vertical(g3)
    c: Coincident(g0,g-1)
    c: DistanceX(g0,g0) = 600
    c: DistanceY(g3,g3) = 180
    c: Radius(g4) = 60
    c: Radius(g5) = 60
    c: Coincident(g6,g4)
    c: PointOnObject(g6,g3)
    c: Horizontal(g6)
    c: Coincident(g7,g5)
    c: PointOnObject(g7,g1)
    c: Horizontal(g7)
    c: Coincident(g8,g5)
    c: PointOnObject(g8,g0)
    c: Vertical(g8)
    c: Equal(g6,g7)
    c: Coincident(g9,g4)
    c: PointOnObject(g9,g2)
    c: Vertical(g9)
    c: Equal(g9,g8)
    c: DistanceX(g6,g6) = 120
    c: PointOnObject(g4,g7)
FEATURE [PartDesign::Pad] Pad  label="fan_plane_pad"
  AllowMultiFace = false
  Direction = (0,0,1)
  Length = 15
  Length2 = 100
  Profile = -> Sketch
  ReferenceAxis = -> Sketch [N_Axis]
  Suppressed = false
  Type = 0
FEATURE [PartDesign::Body] Body  label="fan_plane_body"
  AllowCompound = false
  Group = -> [Sketch,Pad]
  Origin = -> Origin
  Tip = -> Pad
---- part front.FCStd = doc fcstd_43f23b73bbb8 ----
FCSTD DOCUMENT  (FreeCAD 1.0R39319 (Git))
Label: front
License: All rights reserved
LicenseURL: http://en.wikipedia.org/wiki/All_rights_reserved
objects: Sketcher::SketchObject×1, PartDesign::Pad×1, PartDesign::Body×1
note: 6 computed .brp shape members not serialized (recipe doc carries the construction recipe); baked Part::Feature solids carry a one-line shape summary decoded from their .brp

FEATURE [Sketcher::SketchObject] Sketch  label="front_sketch"
  ArcFitTolerance = 0
  AttachmentSupport = -> [YZ_Plane]
  FullyConstrained = true
  MakeInternals = false
  MapMode = 5
  Placement = pos=(0,0,0) rot=(0.57735,0.57735,0.57735;2.0944rad)
  sketch-geometry (4):
    g0: LineSegment StartX=0 StartY=0 StartZ=0 EndX=600 EndY=0 EndZ=0
    g1: LineSegment StartX=600 StartY=0 StartZ=0 EndX=600 EndY=850 EndZ=0
    g2: LineSegment StartX=600 StartY=850 StartZ=0 EndX=0 EndY=850 EndZ=0
    g3: LineSegment StartX=0 StartY=850 StartZ=0 EndX=0 EndY=0 EndZ=0
  constraints (11):
    c: Coincident(g0,g1)
    c: Coincident(g1,g2)
    c: Coincident(g2,g3)
    c: Coincident(g3,g0)
    c: Horizontal(g0)
    c: Horizontal(g2)
    c: Vertical(g1)
    c: Vertical(g3)
    c: Coincident(g0,g-1)
    c: DistanceX(g0,g0) = 600
    c: DistanceY(g3,g3) = 850
FEATURE [PartDesign::Pad] Pad  label="front_pad"
  AllowMultiFace = false
  Direction = (1,-1.129e-13,1.129e-13)
  Length = 15
  Length2 = 100
  Placement = pos=(0,0,0) rot=(0.57735,0.57735,0.57735;2.0944rad)
  Profile = -> Sketch
  Suppressed = false
  Type = 0
FEATURE [PartDesign::Body] Body  label="front_body"
  AllowCompound = false
  Group = -> [Sketch,Pad]
  Origin = -> Origin
  Tip = -> Pad
---- part glass.FCStd = doc fcstd_3278d291d9e2 ----
FCSTD DOCUMENT  (FreeCAD 1.0R39319 (Git))
Label: glass
License: All rights reserved
LicenseURL: https://en.wikipedia.org/wiki/All_rights_reserved
objects: Sketcher::SketchObject×1, PartDesign::Pad×1, PartDesign::Body×1
note: 6 computed .brp shape members not serialized (recipe doc carries the construction recipe); baked Part::Feature solids carry a one-line shape summary decoded from their .brp

FEATURE [Sketcher::SketchObject] Sketch  label="glass_s"
  ArcFitTolerance = 1e-06
  AttachmentSupport = -> [XY_Plane]
  FullyConstrained = true
  MakeInternals = false
  MapMode = 5
  sketch-geometry (16):
    g0: LineSegment StartX=0 StartY=0 StartZ=0 EndX=600 EndY=0 EndZ=0
    g1: LineSegment StartX=600 StartY=0 StartZ=0 EndX=600 EndY=620 EndZ=0
    g2: LineSegment StartX=600 StartY=620 StartZ=0 EndX=0 EndY=620 EndZ=0
    g3: LineSegment StartX=0 StartY=620 StartZ=0 EndX=0 EndY=0 EndZ=0
    g4: Circle CenterX=40 CenterY=580 CenterZ=0 NormalX=0 NormalY=0 NormalZ=1 AngleXU=0 Radius=2
    g5: Circle CenterX=560 CenterY=580 CenterZ=0 NormalX=0 NormalY=0 NormalZ=1 AngleXU=0 Radius=2
    g6: Circle CenterX=560 CenterY=40 CenterZ=0 NormalX=0 NormalY=0 NormalZ=1 AngleXU=0 Radius=2
    g7: Circle CenterX=40 CenterY=40 CenterZ=0 NormalX=0 NormalY=0 NormalZ=1 AngleXU=0 Radius=2
    g8: LineSegment [constr] StartX=40 StartY=580 StartZ=0 EndX=40 EndY=40 EndZ=0
    g9: LineSegment [constr] StartX=40 StartY=40 StartZ=0 EndX=560 EndY=40 EndZ=0
    g10: LineSegment [constr] StartX=560 StartY=40 StartZ=0 EndX=560 EndY=580 EndZ=0
    g11: LineSegment [constr] StartX=560 StartY=580 StartZ=0 EndX=40 EndY=580 EndZ=0
    g12: LineSegment [constr] StartX=560 StartY=580 StartZ=0 EndX=560 EndY=620 EndZ=0
    g13: LineSegment [constr] StartX=560 StartY=580 StartZ=0 EndX=600 EndY=580 EndZ=0
    g14: LineSegment [constr] StartX=40 StartY=40 StartZ=0 EndX=40 EndY=0 EndZ=0
    g15: LineSegment [constr] StartX=40 StartY=40 StartZ=0 EndX=0 EndY=40 EndZ=0
  constraints (43):
    c: Coincident(g0,g1)
    c: Coincident(g1,g2)
    c: Coincident(g2,g3)
    c: Coincident(g3,g0)
    c: Horizontal(g0)
    c: Horizontal(g2)
    c: Vertical(g1)
    c: Vertical(g3)
    c: Coincident(g0,g-1)
    c: DistanceY(g3,g3) = 620
    c: DistanceX(g2,g2) = 600
    c: Coincident(g8,g9)
    c: Coincident(g9,g10)
    c: Coincident(g10,g11)
    c: Coincident(g11,g8)
    c: Vertical(g8)
    c: Vertical(g10)
    c: Horizontal(g9)
    c: Horizontal(g11)
    c: Coincident(g8,g4)
    c: Coincident(g9,g6)
    c: Coincident(g7,g8)
    c: Coincident(g10,g5)
    c: Diameter(g4) = 4
    c: Equal(g4,g7)
    c: Equal(g7,g6)
    c: Equal(g6,g5)
    c: DistanceX(g0,g7) = 40
    c: Coincident(g12,g5)
    c: PointOnObject(g12,g2)
    c: Vertical(g12)
    c: PointOnObject(g13,g1)
    c: Horizontal(g13)
    c: Coincident(g13,g5)
    c: Coincident(g14,g7)
    c: PointOnObject(g14,g0)
    c: Vertical(g14)
    c: Coincident(g15,g7)
    c: PointOnObject(g15,g3)
    c: Horizontal(g15)
    c: Equal(g14,g15)
    c: Equal(g15,g13)
    c: Equal(g13,g12)
FEATURE [PartDesign::Pad] Pad
  Direction = (0,0,1)
  Length = 6
  Length2 = 10
  Profile = -> Sketch
  ReferenceAxis = -> Sketch [N_Axis]
  Refine = true
  Suppressed = false
  Type = 0
FEATURE [PartDesign::Body] Body
  AllowCompound = false
  Group = -> [Sketch,Pad]
  Origin = -> Origin
  Tip = -> Pad
---- part internal_plate.FCStd = doc fcstd_99b1a04e4583 ----
FCSTD DOCUMENT  (FreeCAD 1.0R39319 (Git))
Label: internal_plate
License: All rights reserved
LicenseURL: https://en.wikipedia.org/wiki/All_rights_reserved
objects: Sketcher::SketchObject×1, PartDesign::Pad×1, PartDesign::Body×1
note: 6 computed .brp shape members not serialized (recipe doc carries the construction recipe); baked Part::Feature solids carry a one-line shape summary decoded from their .brp

FEATURE [Sketcher::SketchObject] Sketch  label="internal_plate_s"
  ArcFitTolerance = 1e-06
  AttachmentSupport = -> [XZ_Plane]
  FullyConstrained = true
  MakeInternals = false
  MapMode = 5
  Placement = pos=(0,0,0) rot=(1,0,0;1.5708rad)
  sketch-geometry (4):
    g0: LineSegment StartX=0 StartY=0 StartZ=0 EndX=600 EndY=0 EndZ=0
    g1: LineSegment StartX=600 StartY=0 StartZ=0 EndX=600 EndY=220 EndZ=0
    g2: LineSegment StartX=600 StartY=220 StartZ=0 EndX=0 EndY=220 EndZ=0
    g3: LineSegment StartX=0 StartY=220 StartZ=0 EndX=0 EndY=0 EndZ=0
  constraints (11):
    c: Coincident(g0,g1)
    c: Coincident(g1,g2)
    c: Coincident(g2,g3)
    c: Coincident(g3,g0)
    c: Horizontal(g0)
    c: Horizontal(g2)
    c: Vertical(g1)
    c: Vertical(g3)
    c: Coincident(g0,g-1)
    c: DistanceX(g2,g2) = 600
    c: DistanceY(g3,g3) = 220
FEATURE [PartDesign::Pad] Pad  label="internal_plate"
  Direction = (0,-1,2e-16)
  Length = 15
  Length2 = 10
  Placement = pos=(0,0,0) rot=(1,0,0;1.5708rad)
  Profile = -> Sketch
  ReferenceAxis = -> Sketch [N_Axis]
  Refine = true
  Suppressed = false
  Type = 0
FEATURE [PartDesign::Body] Body  label="internal_plate_body"
  AllowCompound = false
  Group = -> [Sketch,Pad]
  Origin = -> Origin
  Tip = -> Pad
---- part internal_separator.FCStd = doc fcstd_7046e4c8f03f ----
FCSTD DOCUMENT  (FreeCAD 1.0R39319 (Git))
Label: internal_separator
License: All rights reserved
LicenseURL: https://en.wikipedia.org/wiki/All_rights_reserved
objects: Sketcher::SketchObject×1, PartDesign::Pad×1, PartDesign::Body×1
note: 6 computed .brp shape members not serialized (recipe doc carries the construction recipe); baked Part::Feature solids carry a one-line shape summary decoded from their .brp

FEATURE [Sketcher::SketchObject] Sketch  label="internal_separator_s"
  ArcFitTolerance = 1e-06
  AttachmentSupport = -> [XZ_Plane]
  FullyConstrained = true
  MakeInternals = false
  MapMode = 5
  Placement = pos=(0,0,0) rot=(1,0,0;1.5708rad)
  sketch-geometry (4):
    g0: LineSegment StartX=0 StartY=0 StartZ=0 EndX=600 EndY=0 EndZ=0
    g1: LineSegment StartX=600 StartY=0 StartZ=0 EndX=600 EndY=500 EndZ=0
    g2: LineSegment StartX=600 StartY=500 StartZ=0 EndX=0 EndY=500 EndZ=0
    g3: LineSegment StartX=0 StartY=500 StartZ=0 EndX=0 EndY=0 EndZ=0
  constraints (11):
    c: Coincident(g0,g1)
    c: Coincident(g1,g2)
    c: Coincident(g2,g3)
    c: Coincident(g3,g0)
    c: Horizontal(g0)
    c: Horizontal(g2)
    c: Vertical(g1)
    c: Vertical(g3)
    c: Coincident(g0,g-1)
    c: DistanceX(g2,g2) = 600
    c: DistanceY(g3,g3) = 500
FEATURE [PartDesign::Pad] Pad  label="internal_separator"
  Direction = (0,-1,2e-16)
  Length = 15
  Length2 = 10
  Placement = pos=(0,0,0) rot=(1,0,0;1.5708rad)
  Profile = -> Sketch
  ReferenceAxis = -> Sketch [N_Axis]
  Refine = true
  Suppressed = false
  Type = 0
FEATURE [PartDesign::Body] Body  label="internal_separator_body"
  AllowCompound = false
  Group = -> [Sketch,Pad]
  Origin = -> Origin
  Tip = -> Pad
---- part marquee.FCStd = doc fcstd_55bfe33dd053 ----
FCSTD DOCUMENT  (FreeCAD 1.0R39319 (Git))
Label: marquee
License: All rights reserved
LicenseURL: http://en.wikipedia.org/wiki/All_rights_reserved
objects: Sketcher::SketchObject×1, PartDesign::Pad×1, PartDesign::Fillet×1, PartDesign::Body×1
note: 9 computed .brp shape members not serialized (recipe doc carries the construction recipe); baked Part::Feature solids carry a one-line shape summary decoded from their .brp

FEATURE [Sketcher::SketchObject] Sketch  label="marquee_sketch"
  ArcFitTolerance = 0
  AttachmentSupport = -> [XY_Plane]
  FullyConstrained = true
  MakeInternals = false
  MapMode = 5
  sketch-geometry (4):
    g0: LineSegment StartX=0 StartY=0 StartZ=0 EndX=600 EndY=0 EndZ=0
    g1: LineSegment StartX=600 StartY=0 StartZ=0 EndX=600 EndY=170 EndZ=0
    g2: LineSegment StartX=600 StartY=170 StartZ=0 EndX=0 EndY=170 EndZ=0
    g3: LineSegment StartX=0 StartY=170 StartZ=0 EndX=0 EndY=0 EndZ=0
  constraints (11):
    c: Coincident(g0,g1)
    c: Coincident(g1,g2)
    c: Coincident(g2,g3)
    c: Coincident(g3,g0)
    c: Horizontal(g0)
    c: Horizontal(g2)
    c: Vertical(g1)
    c: Vertical(g3)
    c: Coincident(g0,g-1)
    c: DistanceX(g0,g0) = 600
    c: DistanceY(g3,g3) = 170
FEATURE [PartDesign::Pad] Pad  label="marquee_pad"
  AllowMultiFace = false
  Direction = (0,0,1)
  Length = 10
  Length2 = 100
  Profile = -> Sketch
  ReferenceAxis = -> Sketch [N_Axis]
  Suppressed = false
  Type = 0
FEATURE [PartDesign::Fillet] Fillet
  Base = -> Pad [Edge4,Edge10]
  BaseFeature = -> Pad
  Radius = 9
  Refine = true
  SupportTransform = false
  Suppressed = false
  UseAllEdges = false
FEATURE [PartDesign::Body] Body  label="marquee_body"
  AllowCompound = false
  Group = -> [Sketch,Pad,Fillet]
  Origin = -> Origin
  Tip = -> Fillet
---- part side.FCStd = doc fcstd_a7a22d88708c ----
FCSTD DOCUMENT  (FreeCAD 1.0R39319 (Git))
Label: side
License: All rights reserved
LicenseURL: http://en.wikipedia.org/wiki/All_rights_reserved
objects: TechDraw::DrawViewDimension×5, PartDesign::Fillet×2, Sketcher::SketchObject×1, PartDesign::Pad×1, PartDesign::Body×1, TechDraw::DrawSVGTemplate×1, TechDraw::DrawViewPart×1, TechDraw::DrawPage×1
note: 12 computed .brp shape members not serialized (recipe doc carries the construction recipe); baked Part::Feature solids carry a one-line shape summary decoded from their .brp

FEATURE [Sketcher::SketchObject] Sketch  label="side_sketch"
  ArcFitTolerance = 0
  AttachmentSupport = -> [XZ_Plane]
  FullyConstrained = true
  MakeInternals = false
  MapMode = 5
  Placement = pos=(0,0,0) rot=(1,0,0;1.5708rad)
  sketch-geometry (14):
    g0: LineSegment StartX=0 StartY=0 StartZ=0 EndX=0 EndY=1550 EndZ=0
    g1: LineSegment StartX=0 StartY=0 StartZ=0 EndX=450 EndY=0 EndZ=0
    g2: LineSegment StartX=450 StartY=0 StartZ=0 EndX=493.498 EndY=830 EndZ=0
    g3: LineSegment StartX=570 StartY=860 StartZ=0 EndX=590 EndY=1000 EndZ=0
    g4: LineSegment StartX=590 StartY=1000 StartZ=0 EndX=392.01 EndY=1028.28 EndZ=0
    g5: LineSegment StartX=0 StartY=1550 StartZ=0 EndX=150 EndY=1700 EndZ=0
    g6: LineSegment StartX=150 StartY=1700 StartZ=0 EndX=331.508 EndY=1700 EndZ=0
    g7: LineSegment StartX=331.508 StartY=1700 StartZ=0 EndX=362.764 EndY=1522.73 EndZ=0
    g8: LineSegment [constr] StartX=590 StartY=1000 StartZ=0 EndX=0 EndY=1000 EndZ=0
    g9: LineSegment [constr] StartX=570 StartY=860 StartZ=0 EndX=0 EndY=860 EndZ=0
    g10: LineSegment StartX=493.498 StartY=830 StartZ=0 EndX=570 EndY=860 EndZ=0
    g11: LineSegment StartX=392.01 StartY=1028.28 StartZ=0 EndX=258.518 EndY=1468.49 EndZ=0
    g12: LineSegment StartX=362.764 StartY=1522.73 StartZ=0 EndX=312.764 EndY=1522.73 EndZ=0
    g13: LineSegment StartX=312.764 StartY=1522.73 StartZ=0 EndX=258.518 EndY=1468.49 EndZ=0
  constraints (41):
    c: Coincident(g1,g0)
    c: Horizontal(g1)
    c: Coincident(g2,g1)
    c: Coincident(g4,g3)
    c: Coincident(g5,g0)
    c: Coincident(g6,g5)
    c: Coincident(g7,g6)
    c: DistanceY(g1,g6) = 1700
    c: Coincident(g8,g3)
    c: PointOnObject(g8,g0)
    c: Horizontal(g8)
    c: DistanceX(g8,g8) = 590
    c: Coincident(g9,g3)
    c: PointOnObject(g9,g0)
    c: Horizontal(g9)
    c: DistanceX(g9,g9) = 570
    c: DistanceY(g3,g3) = 140
    c: DistanceY(g1,g3) = 1000
    c: Distance(g7) = 180
    c: Distance(g4) = 200
    c: Perpendicular(g3,g4)
    c: Angle(g2,g1) = 1.62316
    c: DistanceY(g2,g2) = 830
    c: Coincident(g0,g-1)
    c: DistanceX(g1,g1) = 450
    c: Coincident(g10,g2)
    c: Coincident(g10,g3)
    c: Coincident(g11,g4)
    c: Horizontal(g6)
    c: Vertical(g0)
    c: DistanceY(g0,g0) = 1550
    c: Angle(g4,g11) = 2.00713
    c: Angle(g6,g7) = 1.74533
    c: Coincident(g12,g7)
    c: Horizontal(g12)
    c: Coincident(g13,g11)
    c: Parallel(g13,g5)
    c: Coincident(g13,g12)
    c: DistanceX(g12,g12) = 50
    c: Distance(g11) = 460
    c: Angle(g0,g5) = 2.35619
FEATURE [PartDesign::Pad] Pad  label="side_pad"
  AllowMultiFace = false
  Direction = (0,-1,-1.035e-13)
  Length = 16
  Length2 = 100
  Placement = pos=(0,0,0) rot=(1,0,0;1.5708rad)
  Profile = -> Sketch
  Suppressed = false
  Type = 0
FEATURE [PartDesign::Fillet] Fillet  label="acute_fillet"
  Base = -> Pad [Edge17,Edge14,Edge11,Edge8,Edge5,Edge1,Edge29,Edge32]
  BaseFeature = -> Pad
  Placement = pos=(0,0,0) rot=(1,0,0;1.5708rad)
  Radius = 25
  Refine = true
  SupportTransform = false
  Suppressed = false
  UseAllEdges = false
FEATURE [PartDesign::Fillet] Fillet001  label="obtuse_fillet"
  Base = -> Fillet [Edge3,Edge52,Edge54,Edge56]
  BaseFeature = -> Fillet
  Placement = pos=(0,0,0) rot=(1,0,0;1.5708rad)
  Radius = 25
  Refine = true
  SupportTransform = false
  Suppressed = false
  UseAllEdges = false
FEATURE [PartDesign::Body] Body  label="side_body"
  AllowCompound = false
  Group = -> [Sketch,Pad,Fillet,Fillet001]
  Origin = -> Origin
  Tip = -> Fillet001
FEATURE [TechDraw::DrawSVGTemplate] Template
  Height = 1720
  Orientation = 0
  Width = 600
FEATURE [TechDraw::DrawViewPart] View
  CoarseView = false
  Direction = (0,1,0)
  Focus = 100
  HardHidden = false
  IsoCount = 0
  IsoHidden = false
  IsoVisible = false
  LockPosition = false
  Perspective = false
  Rotation = 0
  ScaleType = 0
  ScrubCount = 1
  SeamHidden = false
  SeamVisible = false
  SmoothHidden = false
  SmoothVisible = false
  Source = -> [Fillet001]
  X = 300
  XDirection = (-1,0,0)
  Y = 860
FEATURE [TechDraw::DrawViewDimension] Dimension
  AngleOverride = false
  Arbitrary = false
  ArbitraryTolerances = false
  EqualTolerance = false
  ExtensionAngle = 0
  FormatSpec = %.2f
  FormatSpecOverTolerance = %+.2w
  FormatSpecUnderTolerance = %+.2w
  Inverted = false
  LineAngle = 0
  LockPosition = false
  MeasureType = 1
  OverTolerance = 0
  References2D = -> [View]
  Rotation = 0
  ScaleType = 0
  TheoreticalExact = false
  Type = 1
  UnderTolerance = 0
  X = 130.405
  Y = -812.173
FEATURE [TechDraw::DrawViewDimension] Dimension002
  AngleOverride = false
  Arbitrary = false
  ArbitraryTolerances = false
  EqualTolerance = false
  ExtensionAngle = 0
  FormatSpec = %.2f
  FormatSpecOverTolerance = %+.2w
  FormatSpecUnderTolerance = %+.2w
  Inverted = false
  LineAngle = 0
  LockPosition = false
  MeasureType = 1
  OverTolerance = 0
  References2D = -> [View]
  Rotation = 0
  ScaleType = 0
  TheoreticalExact = false
  Type = 0
  UnderTolerance = 0
  X = -219.017
  Y = -325.499
FEATURE [TechDraw::DrawViewDimension] Dimension003
  AngleOverride = false
  Arbitrary = false
  ArbitraryTolerances = false
  EqualTolerance = false
  ExtensionAngle = 0
  FormatSpec = %.2f
  FormatSpecOverTolerance = %+.2w
  FormatSpecUnderTolerance = %+.2w
  Inverted = false
  LineAngle = 0
  LockPosition = false
  MeasureType = 1
  OverTolerance = 0
  References2D = -> [View]
  Rotation = 0
  ScaleType = 0
  TheoreticalExact = false
  Type = 0
  UnderTolerance = 0
  X = -66.9516
  Y = 0
FEATURE [TechDraw::DrawViewDimension] Dimension004
  AngleOverride = false
  Arbitrary = false
  ArbitraryTolerances = false
  EqualTolerance = false
  ExtensionAngle = 0
  FormatSpec = %.2f
  FormatSpecOverTolerance = %+.2w
  FormatSpecUnderTolerance = %+.2w
  Inverted = false
  LineAngle = 0
  LockPosition = false
  MeasureType = 1
  OverTolerance = 0
  References2D = -> [View]
  Rotation = 0
  ScaleType = 0
  TheoreticalExact = false
  Type = 2
  UnderTolerance = 0
  X = 230.057
  Y = 7.83477
FEATURE [TechDraw::DrawViewDimension] Dimension005
  AngleOverride = false
  Arbitrary = false
  ArbitraryTolerances = false
  EqualTolerance = false
  ExtensionAngle = 0
  FormatSpec = %.2f
  FormatSpecOverTolerance = %+.2w
  FormatSpecUnderTolerance = %+.2w
  Inverted = false
  LineAngle = 0
  LockPosition = false
  MeasureType = 1
  OverTolerance = 0
  References2D = -> [View]
  Rotation = 0
  ScaleType = 0
  TheoreticalExact = false
  Type = 1
  UnderTolerance = 0
  X = 78.7038
  Y = 765.314
FEATURE [TechDraw::DrawPage] Page
  KeepUpdated = true
  NextBalloonIndex = 1
  ProjectionType = 0
  Template = -> Template
  Views = -> [View,Dimension,Dimension002,Dimension003,Dimension004,Dimension005]
---- part speaker_panel.FCStd = doc fcstd_4d9cbf6318f5 ----
FCSTD DOCUMENT  (FreeCAD 1.0R39319 (Git))
Label: speaker_panel
License: All rights reserved
LicenseURL: http://en.wikipedia.org/wiki/All_rights_reserved
objects: Sketcher::SketchObject×1, PartDesign::Pad×1, PartDesign::Body×1
note: 6 computed .brp shape members not serialized (recipe doc carries the construction recipe); baked Part::Feature solids carry a one-line shape summary decoded from their .brp

FEATURE [Sketcher::SketchObject] Sketch  label="speaker_sketch"
  ArcFitTolerance = 0
  AttachmentSupport = -> [XY_Plane]
  FullyConstrained = true
  MakeInternals = false
  MapMode = 5
  sketch-geometry (10):
    g0: LineSegment StartX=0 StartY=0 StartZ=0 EndX=600 EndY=0 EndZ=0
    g1: LineSegment StartX=600 StartY=0 StartZ=0 EndX=600 EndY=160 EndZ=0
    g2: LineSegment StartX=600 StartY=160 StartZ=0 EndX=0 EndY=160 EndZ=0
    g3: LineSegment StartX=0 StartY=160 StartZ=0 EndX=0 EndY=0 EndZ=0
    g4: Circle CenterX=70 CenterY=70 CenterZ=0 NormalX=0 NormalY=0 NormalZ=1 AngleXU=0 Radius=40
    g5: Circle CenterX=530 CenterY=70 CenterZ=0 NormalX=0 NormalY=0 NormalZ=1 AngleXU=0 Radius=40
    g6: LineSegment [constr] StartX=70 StartY=70 StartZ=0 EndX=70 EndY=0 EndZ=0
    g7: LineSegment [constr] StartX=70 StartY=70 StartZ=0 EndX=0 EndY=70 EndZ=0
    g8: LineSegment [constr] StartX=530 StartY=70 StartZ=0 EndX=600 EndY=70 EndZ=0
    g9: LineSegment [constr] StartX=530 StartY=70 StartZ=0 EndX=530 EndY=0 EndZ=0
  constraints (29):
    c: Coincident(g0,g1)
    c: Coincident(g1,g2)
    c: Coincident(g2,g3)
    c: Coincident(g3,g0)
    c: Horizontal(g0)
    c: Horizontal(g2)
    c: Vertical(g1)
    c: Vertical(g3)
    c: Coincident(g0,g-1)
    c: DistanceX(g0,g0) = 600
    c: DistanceY(g3,g3) = 160
    c: Radius(g4) = 40
    c: Radius(g5) = 40
    c: Coincident(g6,g4)
    c: PointOnObject(g6,g0)
    c: Vertical(g6)
    c: PointOnObject(g7,g3)
    c: Horizontal(g7)
    c: Coincident(g8,g5)
    c: PointOnObject(g8,g1)
    c: Horizontal(g8)
    c: Coincident(g9,g5)
    c: PointOnObject(g9,g0)
    c: Vertical(g9)
    c: Equal(g7,g8)
    c: Coincident(g7,g4)
    c: Equal(g6,g9)
    c: DistanceX(g7,g7) = 70
    c: DistanceY(g6,g6) = 70
FEATURE [PartDesign::Pad] Pad  label="speaker_panel_pad"
  AllowMultiFace = false
  Direction = (0,0,1)
  Length = 15
  Length2 = 100
  Profile = -> Sketch
  ReferenceAxis = -> Sketch [N_Axis]
  Suppressed = false
  Type = 0
FEATURE [PartDesign::Body] Body  label="speaker_panel_body"
  AllowCompound = false
  Group = -> [Sketch,Pad]
  Origin = -> Origin
  Tip = -> Pad
---- part top.FCStd = doc fcstd_52f9a6688da0 ----
FCSTD DOCUMENT  (FreeCAD 1.0R39319 (Git))
Label: top
License: All rights reserved
LicenseURL: http://en.wikipedia.org/wiki/All_rights_reserved
objects: Sketcher::SketchObject×1, PartDesign::Pad×1, PartDesign::Body×1
note: 6 computed .brp shape members not serialized (recipe doc carries the construction recipe); baked Part::Feature solids carry a one-line shape summary decoded from their .brp

FEATURE [Sketcher::SketchObject] Sketch  label="top_sketch"
  ArcFitTolerance = 0
  AttachmentSupport = -> [XY_Plane]
  FullyConstrained = true
  MakeInternals = false
  MapMode = 5
  sketch-geometry (4):
    g0: LineSegment StartX=0 StartY=0 StartZ=0 EndX=600 EndY=0 EndZ=0
    g1: LineSegment StartX=600 StartY=0 StartZ=0 EndX=600 EndY=170 EndZ=0
    g2: LineSegment StartX=600 StartY=170 StartZ=0 EndX=0 EndY=170 EndZ=0
    g3: LineSegment StartX=0 StartY=170 StartZ=0 EndX=0 EndY=0 EndZ=0
  constraints (11):
    c: Coincident(g0,g1)
    c: Coincident(g1,g2)
    c: Coincident(g2,g3)
    c: Coincident(g3,g0)
    c: Horizontal(g0)
    c: Horizontal(g2)
    c: Vertical(g1)
    c: Vertical(g3)
    c: Coincident(g0,g-1)
    c: DistanceY(g3,g3) = 170
    c: DistanceX(g0,g0) = 600
FEATURE [PartDesign::Pad] Pad  label="top_pad"
  AllowMultiFace = false
  Direction = (0,0,1)
  Length = 15
  Length2 = 100
  Profile = -> Sketch
  ReferenceAxis = -> Sketch [N_Axis]
  Suppressed = false
  Type = 0
FEATURE [PartDesign::Body] Body  label="top_body"
  AllowCompound = false
  Group = -> [Sketch,Pad]
  Origin = -> Origin
  Tip = -> Pad
